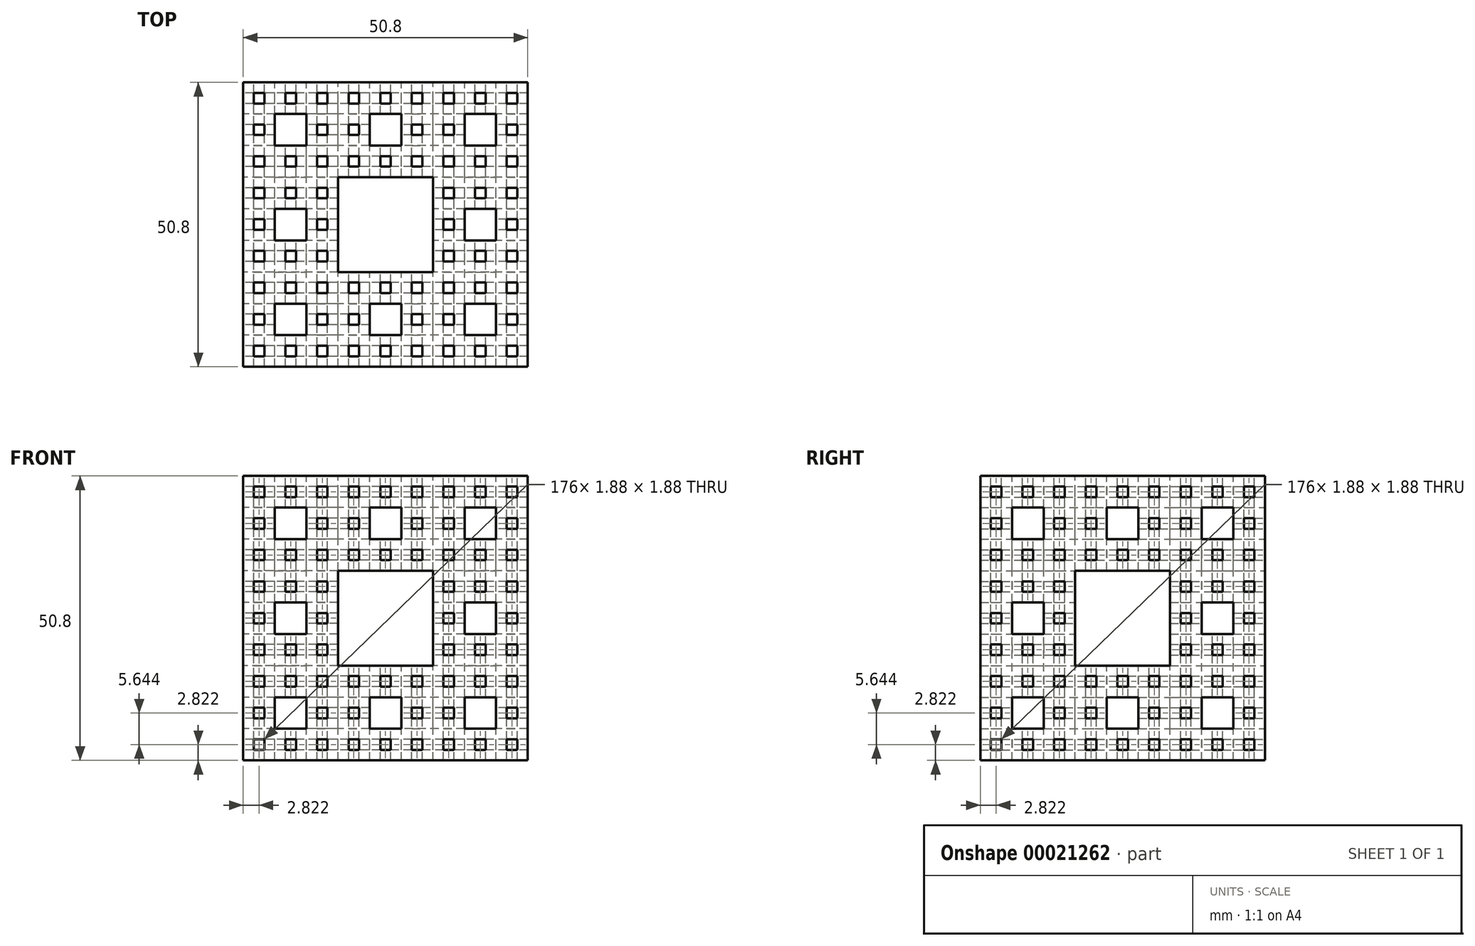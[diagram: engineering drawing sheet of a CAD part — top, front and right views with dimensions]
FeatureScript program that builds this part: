
annotation { "Feature Type Name" : "Feature", "Feature Type Description" : "" }
export const myFeature = defineFeature(function(context is Context, id is Id, definition is map)
    precondition{}
    {
        {
            var Q0;
            Q0=qCreatedBy(makeId("Front.planeOp"),FACE);
            var sketch = newSketch(context, id + "F0", { "sketchPlane" : qUnion([Q0])});
            skLineSegment(sketch, "E0.bottom", {"start": v(0, 0) * mm, "end": v(50.8, 0) * mm});
            skLineSegment(sketch, "E0.top", {"start": v(0, 50.8) * mm, "end": v(50.8, 50.8) * mm});
            skLineSegment(sketch, "E0.left", {"start": v(0, 0) * mm, "end": v(0, 50.8) * mm});
            skLineSegment(sketch, "E0.right", {"start": v(50.8, 0) * mm, "end": v(50.8, 50.8) * mm});
            skSolve(sketch);
        }
        {
            var Q0;
            Q0=makeQuery(id+"F0.imprint","IMPRINT",FACE,{"disambiguationData":[TD([[makeQuery(id+"F0.imprint","IMPRINT",EDGE,{"derivedFrom":sQuery(id+"F0.wireOp",EDGE,"E0.bottom")}),1.0]])]});
            extrude(context, id + "F1", {"entities" : qUnion([Q0]), "depth" : 50.8 * mm});
        }
        {
            var Q0;
            Q0=makeQuery(id+"F1.opExtrude","CAP_FACE",FACE,{"disambiguationData":[OSD([sQuery(id+"F0.wireOp",EDGE,"E0.bottom"),sQuery(id+"F0.wireOp",EDGE,"E0.top"),sQuery(id+"F0.wireOp",EDGE,"E0.left"),sQuery(id+"F0.wireOp",EDGE,"E0.right")])],"isStart":true});
            var sketch = newSketch(context, id + "F2", { "sketchPlane" : qUnion([Q0])});
            skLineSegment(sketch, "E1.bottom", {"start": v(-33.87, 33.87) * mm, "end": v(-16.93, 33.87) * mm});
            skLineSegment(sketch, "E1.top", {"start": v(-33.87, 16.93) * mm, "end": v(-16.93, 16.93) * mm});
            skLineSegment(sketch, "E1.left", {"start": v(-33.87, 33.87) * mm, "end": v(-33.87, 16.93) * mm});
            skLineSegment(sketch, "E1.right", {"start": v(-16.93, 33.87) * mm, "end": v(-16.93, 16.93) * mm});
            skLineSegment(sketch, "E2.bottom", {"start": v(-45.16, 11.29) * mm, "end": v(-39.51, 11.29) * mm});
            skLineSegment(sketch, "E2.top", {"start": v(-45.16, 5.64) * mm, "end": v(-39.51, 5.64) * mm});
            skLineSegment(sketch, "E2.left", {"start": v(-45.16, 11.29) * mm, "end": v(-45.16, 5.64) * mm});
            skLineSegment(sketch, "E2.right", {"start": v(-39.51, 11.29) * mm, "end": v(-39.51, 5.64) * mm});
            skLineSegment(sketch, "E3.bottom", {"start": v(-48.92, 3.76) * mm, "end": v(-47.04, 3.76) * mm});
            skLineSegment(sketch, "E3.top", {"start": v(-48.92, 1.88) * mm, "end": v(-47.04, 1.88) * mm});
            skLineSegment(sketch, "E3.left", {"start": v(-48.92, 3.76) * mm, "end": v(-48.92, 1.88) * mm});
            skLineSegment(sketch, "E3.right", {"start": v(-47.04, 3.76) * mm, "end": v(-47.04, 1.88) * mm});
            skLineSegment(sketch, "E4.0.1.0", {"start": v(-39.51, 28.22) * mm, "end": v(-39.51, 22.58) * mm});
            skLineSegment(sketch, "E4.0.1.5", {"start": v(-45.16, 28.22) * mm, "end": v(-39.51, 28.22) * mm});
            skLineSegment(sketch, "E4.0.1.6", {"start": v(-45.16, 22.58) * mm, "end": v(-39.51, 22.58) * mm});
            skLineSegment(sketch, "E4.0.1.7", {"start": v(-45.16, 28.22) * mm, "end": v(-45.16, 22.58) * mm});
            skLineSegment(sketch, "E4.0.2.0", {"start": v(-39.51, 45.16) * mm, "end": v(-39.51, 39.51) * mm});
            skLineSegment(sketch, "E4.0.2.5", {"start": v(-45.16, 45.16) * mm, "end": v(-39.51, 45.16) * mm});
            skLineSegment(sketch, "E4.0.2.6", {"start": v(-45.16, 39.51) * mm, "end": v(-39.51, 39.51) * mm});
            skLineSegment(sketch, "E4.0.2.7", {"start": v(-45.16, 45.16) * mm, "end": v(-45.16, 39.51) * mm});
            skLineSegment(sketch, "E4.1.0.0", {"start": v(-22.58, 11.29) * mm, "end": v(-22.58, 5.64) * mm});
            skLineSegment(sketch, "E4.1.0.5", {"start": v(-28.22, 11.29) * mm, "end": v(-22.58, 11.29) * mm});
            skLineSegment(sketch, "E4.1.0.6", {"start": v(-28.22, 5.64) * mm, "end": v(-22.58, 5.64) * mm});
            skLineSegment(sketch, "E4.1.0.7", {"start": v(-28.22, 11.29) * mm, "end": v(-28.22, 5.64) * mm});
            skLineSegment(sketch, "E4.1.2.0", {"start": v(-22.58, 45.16) * mm, "end": v(-22.58, 39.51) * mm});
            skLineSegment(sketch, "E4.1.2.5", {"start": v(-28.22, 45.16) * mm, "end": v(-22.58, 45.16) * mm});
            skLineSegment(sketch, "E4.1.2.6", {"start": v(-28.22, 39.51) * mm, "end": v(-22.58, 39.51) * mm});
            skLineSegment(sketch, "E4.1.2.7", {"start": v(-28.22, 45.16) * mm, "end": v(-28.22, 39.51) * mm});
            skLineSegment(sketch, "E4.2.0.0", {"start": v(-5.64, 11.29) * mm, "end": v(-5.64, 5.64) * mm});
            skLineSegment(sketch, "E4.2.0.5", {"start": v(-11.29, 11.29) * mm, "end": v(-5.64, 11.29) * mm});
            skLineSegment(sketch, "E4.2.0.6", {"start": v(-11.29, 5.64) * mm, "end": v(-5.64, 5.64) * mm});
            skLineSegment(sketch, "E4.2.0.7", {"start": v(-11.29, 11.29) * mm, "end": v(-11.29, 5.64) * mm});
            skLineSegment(sketch, "E4.2.1.0", {"start": v(-5.64, 28.22) * mm, "end": v(-5.64, 22.58) * mm});
            skLineSegment(sketch, "E4.2.1.5", {"start": v(-11.29, 28.22) * mm, "end": v(-5.64, 28.22) * mm});
            skLineSegment(sketch, "E4.2.1.6", {"start": v(-11.29, 22.58) * mm, "end": v(-5.64, 22.58) * mm});
            skLineSegment(sketch, "E4.2.1.7", {"start": v(-11.29, 28.22) * mm, "end": v(-11.29, 22.58) * mm});
            skLineSegment(sketch, "E4.2.2.0", {"start": v(-5.64, 45.16) * mm, "end": v(-5.64, 39.51) * mm});
            skLineSegment(sketch, "E4.2.2.5", {"start": v(-11.29, 45.16) * mm, "end": v(-5.64, 45.16) * mm});
            skLineSegment(sketch, "E4.2.2.6", {"start": v(-11.29, 39.51) * mm, "end": v(-5.64, 39.51) * mm});
            skLineSegment(sketch, "E4.2.2.7", {"start": v(-11.29, 45.16) * mm, "end": v(-11.29, 39.51) * mm});
            skLineSegment(sketch, "E4.direction1", {"start": v(-39.51, 5.64) * mm, "end": v(-22.58, 5.64) * mm, "construction": true});
            skLineSegment(sketch, "E4.direction2", {"start": v(-39.51, 5.64) * mm, "end": v(-39.51, 22.58) * mm, "construction": true});
            skLineSegment(sketch, "E5.0.1.2", {"start": v(-48.92, 9.4) * mm, "end": v(-47.04, 9.4) * mm});
            skLineSegment(sketch, "E5.0.1.3", {"start": v(-48.92, 7.53) * mm, "end": v(-47.04, 7.53) * mm});
            skLineSegment(sketch, "E5.0.1.4", {"start": v(-48.92, 9.4) * mm, "end": v(-48.92, 7.53) * mm});
            skLineSegment(sketch, "E5.0.1.5", {"start": v(-47.04, 9.4) * mm, "end": v(-47.04, 7.53) * mm});
            skLineSegment(sketch, "E5.0.2.2", {"start": v(-48.92, 15.05) * mm, "end": v(-47.04, 15.05) * mm});
            skLineSegment(sketch, "E5.0.2.3", {"start": v(-48.92, 13.17) * mm, "end": v(-47.04, 13.17) * mm});
            skLineSegment(sketch, "E5.0.2.4", {"start": v(-48.92, 15.05) * mm, "end": v(-48.92, 13.17) * mm});
            skLineSegment(sketch, "E5.0.2.5", {"start": v(-47.04, 15.05) * mm, "end": v(-47.04, 13.17) * mm});
            skLineSegment(sketch, "E5.0.3.2", {"start": v(-48.92, 20.7) * mm, "end": v(-47.04, 20.7) * mm});
            skLineSegment(sketch, "E5.0.3.3", {"start": v(-48.92, 18.81) * mm, "end": v(-47.04, 18.81) * mm});
            skLineSegment(sketch, "E5.0.3.4", {"start": v(-48.92, 20.7) * mm, "end": v(-48.92, 18.81) * mm});
            skLineSegment(sketch, "E5.0.3.5", {"start": v(-47.04, 20.7) * mm, "end": v(-47.04, 18.81) * mm});
            skLineSegment(sketch, "E5.0.4.2", {"start": v(-48.92, 26.34) * mm, "end": v(-47.04, 26.34) * mm});
            skLineSegment(sketch, "E5.0.4.3", {"start": v(-48.92, 24.46) * mm, "end": v(-47.04, 24.46) * mm});
            skLineSegment(sketch, "E5.0.4.4", {"start": v(-48.92, 26.34) * mm, "end": v(-48.92, 24.46) * mm});
            skLineSegment(sketch, "E5.0.4.5", {"start": v(-47.04, 26.34) * mm, "end": v(-47.04, 24.46) * mm});
            skLineSegment(sketch, "E5.0.5.2", {"start": v(-48.92, 31.99) * mm, "end": v(-47.04, 31.99) * mm});
            skLineSegment(sketch, "E5.0.5.3", {"start": v(-48.92, 30.1) * mm, "end": v(-47.04, 30.1) * mm});
            skLineSegment(sketch, "E5.0.5.4", {"start": v(-48.92, 31.99) * mm, "end": v(-48.92, 30.1) * mm});
            skLineSegment(sketch, "E5.0.5.5", {"start": v(-47.04, 31.99) * mm, "end": v(-47.04, 30.1) * mm});
            skLineSegment(sketch, "E5.0.6.2", {"start": v(-48.92, 37.63) * mm, "end": v(-47.04, 37.63) * mm});
            skLineSegment(sketch, "E5.0.6.3", {"start": v(-48.92, 35.75) * mm, "end": v(-47.04, 35.75) * mm});
            skLineSegment(sketch, "E5.0.6.4", {"start": v(-48.92, 37.63) * mm, "end": v(-48.92, 35.75) * mm});
            skLineSegment(sketch, "E5.0.6.5", {"start": v(-47.04, 37.63) * mm, "end": v(-47.04, 35.75) * mm});
            skLineSegment(sketch, "E5.0.7.2", {"start": v(-48.92, 43.27) * mm, "end": v(-47.04, 43.27) * mm});
            skLineSegment(sketch, "E5.0.7.3", {"start": v(-48.92, 41.4) * mm, "end": v(-47.04, 41.4) * mm});
            skLineSegment(sketch, "E5.0.7.4", {"start": v(-48.92, 43.27) * mm, "end": v(-48.92, 41.4) * mm});
            skLineSegment(sketch, "E5.0.7.5", {"start": v(-47.04, 43.27) * mm, "end": v(-47.04, 41.4) * mm});
            skLineSegment(sketch, "E5.0.8.2", {"start": v(-48.92, 48.92) * mm, "end": v(-47.04, 48.92) * mm});
            skLineSegment(sketch, "E5.0.8.3", {"start": v(-48.92, 47.04) * mm, "end": v(-47.04, 47.04) * mm});
            skLineSegment(sketch, "E5.0.8.4", {"start": v(-48.92, 48.92) * mm, "end": v(-48.92, 47.04) * mm});
            skLineSegment(sketch, "E5.0.8.5", {"start": v(-47.04, 48.92) * mm, "end": v(-47.04, 47.04) * mm});
            skLineSegment(sketch, "E5.1.0.2", {"start": v(-43.27, 3.76) * mm, "end": v(-41.4, 3.76) * mm});
            skLineSegment(sketch, "E5.1.0.3", {"start": v(-43.27, 1.88) * mm, "end": v(-41.4, 1.88) * mm});
            skLineSegment(sketch, "E5.1.0.4", {"start": v(-43.27, 3.76) * mm, "end": v(-43.27, 1.88) * mm});
            skLineSegment(sketch, "E5.1.0.5", {"start": v(-41.4, 3.76) * mm, "end": v(-41.4, 1.88) * mm});
            skLineSegment(sketch, "E5.1.2.2", {"start": v(-43.27, 15.05) * mm, "end": v(-41.4, 15.05) * mm});
            skLineSegment(sketch, "E5.1.2.3", {"start": v(-43.27, 13.17) * mm, "end": v(-41.4, 13.17) * mm});
            skLineSegment(sketch, "E5.1.2.4", {"start": v(-43.27, 15.05) * mm, "end": v(-43.27, 13.17) * mm});
            skLineSegment(sketch, "E5.1.2.5", {"start": v(-41.4, 15.05) * mm, "end": v(-41.4, 13.17) * mm});
            skLineSegment(sketch, "E5.1.3.2", {"start": v(-43.27, 20.7) * mm, "end": v(-41.4, 20.7) * mm});
            skLineSegment(sketch, "E5.1.3.3", {"start": v(-43.27, 18.81) * mm, "end": v(-41.4, 18.81) * mm});
            skLineSegment(sketch, "E5.1.3.4", {"start": v(-43.27, 20.7) * mm, "end": v(-43.27, 18.81) * mm});
            skLineSegment(sketch, "E5.1.3.5", {"start": v(-41.4, 20.7) * mm, "end": v(-41.4, 18.81) * mm});
            skLineSegment(sketch, "E5.1.5.2", {"start": v(-43.27, 31.99) * mm, "end": v(-41.4, 31.99) * mm});
            skLineSegment(sketch, "E5.1.5.3", {"start": v(-43.27, 30.1) * mm, "end": v(-41.4, 30.1) * mm});
            skLineSegment(sketch, "E5.1.5.4", {"start": v(-43.27, 31.99) * mm, "end": v(-43.27, 30.1) * mm});
            skLineSegment(sketch, "E5.1.5.5", {"start": v(-41.4, 31.99) * mm, "end": v(-41.4, 30.1) * mm});
            skLineSegment(sketch, "E5.1.6.2", {"start": v(-43.27, 37.63) * mm, "end": v(-41.4, 37.63) * mm});
            skLineSegment(sketch, "E5.1.6.3", {"start": v(-43.27, 35.75) * mm, "end": v(-41.4, 35.75) * mm});
            skLineSegment(sketch, "E5.1.6.4", {"start": v(-43.27, 37.63) * mm, "end": v(-43.27, 35.75) * mm});
            skLineSegment(sketch, "E5.1.6.5", {"start": v(-41.4, 37.63) * mm, "end": v(-41.4, 35.75) * mm});
            skLineSegment(sketch, "E5.1.8.2", {"start": v(-43.27, 48.92) * mm, "end": v(-41.4, 48.92) * mm});
            skLineSegment(sketch, "E5.1.8.3", {"start": v(-43.27, 47.04) * mm, "end": v(-41.4, 47.04) * mm});
            skLineSegment(sketch, "E5.1.8.4", {"start": v(-43.27, 48.92) * mm, "end": v(-43.27, 47.04) * mm});
            skLineSegment(sketch, "E5.1.8.5", {"start": v(-41.4, 48.92) * mm, "end": v(-41.4, 47.04) * mm});
            skLineSegment(sketch, "E5.2.0.2", {"start": v(-37.63, 3.76) * mm, "end": v(-35.75, 3.76) * mm});
            skLineSegment(sketch, "E5.2.0.3", {"start": v(-37.63, 1.88) * mm, "end": v(-35.75, 1.88) * mm});
            skLineSegment(sketch, "E5.2.0.4", {"start": v(-37.63, 3.76) * mm, "end": v(-37.63, 1.88) * mm});
            skLineSegment(sketch, "E5.2.0.5", {"start": v(-35.75, 3.76) * mm, "end": v(-35.75, 1.88) * mm});
            skLineSegment(sketch, "E5.2.1.2", {"start": v(-37.63, 9.4) * mm, "end": v(-35.75, 9.4) * mm});
            skLineSegment(sketch, "E5.2.1.3", {"start": v(-37.63, 7.53) * mm, "end": v(-35.75, 7.53) * mm});
            skLineSegment(sketch, "E5.2.1.4", {"start": v(-37.63, 9.4) * mm, "end": v(-37.63, 7.53) * mm});
            skLineSegment(sketch, "E5.2.1.5", {"start": v(-35.75, 9.4) * mm, "end": v(-35.75, 7.53) * mm});
            skLineSegment(sketch, "E5.2.2.2", {"start": v(-37.63, 15.05) * mm, "end": v(-35.75, 15.05) * mm});
            skLineSegment(sketch, "E5.2.2.3", {"start": v(-37.63, 13.17) * mm, "end": v(-35.75, 13.17) * mm});
            skLineSegment(sketch, "E5.2.2.4", {"start": v(-37.63, 15.05) * mm, "end": v(-37.63, 13.17) * mm});
            skLineSegment(sketch, "E5.2.2.5", {"start": v(-35.75, 15.05) * mm, "end": v(-35.75, 13.17) * mm});
            skLineSegment(sketch, "E5.2.3.2", {"start": v(-37.63, 20.7) * mm, "end": v(-35.75, 20.7) * mm});
            skLineSegment(sketch, "E5.2.3.3", {"start": v(-37.63, 18.81) * mm, "end": v(-35.75, 18.81) * mm});
            skLineSegment(sketch, "E5.2.3.4", {"start": v(-37.63, 20.7) * mm, "end": v(-37.63, 18.81) * mm});
            skLineSegment(sketch, "E5.2.3.5", {"start": v(-35.75, 20.7) * mm, "end": v(-35.75, 18.81) * mm});
            skLineSegment(sketch, "E5.2.4.2", {"start": v(-37.63, 26.34) * mm, "end": v(-35.75, 26.34) * mm});
            skLineSegment(sketch, "E5.2.4.3", {"start": v(-37.63, 24.46) * mm, "end": v(-35.75, 24.46) * mm});
            skLineSegment(sketch, "E5.2.4.4", {"start": v(-37.63, 26.34) * mm, "end": v(-37.63, 24.46) * mm});
            skLineSegment(sketch, "E5.2.4.5", {"start": v(-35.75, 26.34) * mm, "end": v(-35.75, 24.46) * mm});
            skLineSegment(sketch, "E5.2.5.2", {"start": v(-37.63, 31.99) * mm, "end": v(-35.75, 31.99) * mm});
            skLineSegment(sketch, "E5.2.5.3", {"start": v(-37.63, 30.1) * mm, "end": v(-35.75, 30.1) * mm});
            skLineSegment(sketch, "E5.2.5.4", {"start": v(-37.63, 31.99) * mm, "end": v(-37.63, 30.1) * mm});
            skLineSegment(sketch, "E5.2.5.5", {"start": v(-35.75, 31.99) * mm, "end": v(-35.75, 30.1) * mm});
            skLineSegment(sketch, "E5.2.6.2", {"start": v(-37.63, 37.63) * mm, "end": v(-35.75, 37.63) * mm});
            skLineSegment(sketch, "E5.2.6.3", {"start": v(-37.63, 35.75) * mm, "end": v(-35.75, 35.75) * mm});
            skLineSegment(sketch, "E5.2.6.4", {"start": v(-37.63, 37.63) * mm, "end": v(-37.63, 35.75) * mm});
            skLineSegment(sketch, "E5.2.6.5", {"start": v(-35.75, 37.63) * mm, "end": v(-35.75, 35.75) * mm});
            skLineSegment(sketch, "E5.2.7.2", {"start": v(-37.63, 43.27) * mm, "end": v(-35.75, 43.27) * mm});
            skLineSegment(sketch, "E5.2.7.3", {"start": v(-37.63, 41.4) * mm, "end": v(-35.75, 41.4) * mm});
            skLineSegment(sketch, "E5.2.7.4", {"start": v(-37.63, 43.27) * mm, "end": v(-37.63, 41.4) * mm});
            skLineSegment(sketch, "E5.2.7.5", {"start": v(-35.75, 43.27) * mm, "end": v(-35.75, 41.4) * mm});
            skLineSegment(sketch, "E5.2.8.2", {"start": v(-37.63, 48.92) * mm, "end": v(-35.75, 48.92) * mm});
            skLineSegment(sketch, "E5.2.8.3", {"start": v(-37.63, 47.04) * mm, "end": v(-35.75, 47.04) * mm});
            skLineSegment(sketch, "E5.2.8.4", {"start": v(-37.63, 48.92) * mm, "end": v(-37.63, 47.04) * mm});
            skLineSegment(sketch, "E5.2.8.5", {"start": v(-35.75, 48.92) * mm, "end": v(-35.75, 47.04) * mm});
            skLineSegment(sketch, "E5.3.0.2", {"start": v(-31.99, 3.76) * mm, "end": v(-30.1, 3.76) * mm});
            skLineSegment(sketch, "E5.3.0.3", {"start": v(-31.99, 1.88) * mm, "end": v(-30.1, 1.88) * mm});
            skLineSegment(sketch, "E5.3.0.4", {"start": v(-31.99, 3.76) * mm, "end": v(-31.99, 1.88) * mm});
            skLineSegment(sketch, "E5.3.0.5", {"start": v(-30.1, 3.76) * mm, "end": v(-30.1, 1.88) * mm});
            skLineSegment(sketch, "E5.3.1.2", {"start": v(-31.99, 9.4) * mm, "end": v(-30.1, 9.4) * mm});
            skLineSegment(sketch, "E5.3.1.3", {"start": v(-31.99, 7.53) * mm, "end": v(-30.1, 7.53) * mm});
            skLineSegment(sketch, "E5.3.1.4", {"start": v(-31.99, 9.4) * mm, "end": v(-31.99, 7.53) * mm});
            skLineSegment(sketch, "E5.3.1.5", {"start": v(-30.1, 9.4) * mm, "end": v(-30.1, 7.53) * mm});
            skLineSegment(sketch, "E5.3.2.2", {"start": v(-31.99, 15.05) * mm, "end": v(-30.1, 15.05) * mm});
            skLineSegment(sketch, "E5.3.2.3", {"start": v(-31.99, 13.17) * mm, "end": v(-30.1, 13.17) * mm});
            skLineSegment(sketch, "E5.3.2.4", {"start": v(-31.99, 15.05) * mm, "end": v(-31.99, 13.17) * mm});
            skLineSegment(sketch, "E5.3.2.5", {"start": v(-30.1, 15.05) * mm, "end": v(-30.1, 13.17) * mm});
            skLineSegment(sketch, "E5.3.6.2", {"start": v(-31.99, 37.63) * mm, "end": v(-30.1, 37.63) * mm});
            skLineSegment(sketch, "E5.3.6.3", {"start": v(-31.99, 35.75) * mm, "end": v(-30.1, 35.75) * mm});
            skLineSegment(sketch, "E5.3.6.4", {"start": v(-31.99, 37.63) * mm, "end": v(-31.99, 35.75) * mm});
            skLineSegment(sketch, "E5.3.6.5", {"start": v(-30.1, 37.63) * mm, "end": v(-30.1, 35.75) * mm});
            skLineSegment(sketch, "E5.3.7.2", {"start": v(-31.99, 43.27) * mm, "end": v(-30.1, 43.27) * mm});
            skLineSegment(sketch, "E5.3.7.3", {"start": v(-31.99, 41.4) * mm, "end": v(-30.1, 41.4) * mm});
            skLineSegment(sketch, "E5.3.7.4", {"start": v(-31.99, 43.27) * mm, "end": v(-31.99, 41.4) * mm});
            skLineSegment(sketch, "E5.3.7.5", {"start": v(-30.1, 43.27) * mm, "end": v(-30.1, 41.4) * mm});
            skLineSegment(sketch, "E5.3.8.2", {"start": v(-31.99, 48.92) * mm, "end": v(-30.1, 48.92) * mm});
            skLineSegment(sketch, "E5.3.8.3", {"start": v(-31.99, 47.04) * mm, "end": v(-30.1, 47.04) * mm});
            skLineSegment(sketch, "E5.3.8.4", {"start": v(-31.99, 48.92) * mm, "end": v(-31.99, 47.04) * mm});
            skLineSegment(sketch, "E5.3.8.5", {"start": v(-30.1, 48.92) * mm, "end": v(-30.1, 47.04) * mm});
            skLineSegment(sketch, "E5.4.0.2", {"start": v(-26.34, 3.76) * mm, "end": v(-24.46, 3.76) * mm});
            skLineSegment(sketch, "E5.4.0.3", {"start": v(-26.34, 1.88) * mm, "end": v(-24.46, 1.88) * mm});
            skLineSegment(sketch, "E5.4.0.4", {"start": v(-26.34, 3.76) * mm, "end": v(-26.34, 1.88) * mm});
            skLineSegment(sketch, "E5.4.0.5", {"start": v(-24.46, 3.76) * mm, "end": v(-24.46, 1.88) * mm});
            skLineSegment(sketch, "E5.4.2.2", {"start": v(-26.34, 15.05) * mm, "end": v(-24.46, 15.05) * mm});
            skLineSegment(sketch, "E5.4.2.3", {"start": v(-26.34, 13.17) * mm, "end": v(-24.46, 13.17) * mm});
            skLineSegment(sketch, "E5.4.2.4", {"start": v(-26.34, 15.05) * mm, "end": v(-26.34, 13.17) * mm});
            skLineSegment(sketch, "E5.4.2.5", {"start": v(-24.46, 15.05) * mm, "end": v(-24.46, 13.17) * mm});
            skLineSegment(sketch, "E5.4.6.2", {"start": v(-26.34, 37.63) * mm, "end": v(-24.46, 37.63) * mm});
            skLineSegment(sketch, "E5.4.6.3", {"start": v(-26.34, 35.75) * mm, "end": v(-24.46, 35.75) * mm});
            skLineSegment(sketch, "E5.4.6.4", {"start": v(-26.34, 37.63) * mm, "end": v(-26.34, 35.75) * mm});
            skLineSegment(sketch, "E5.4.6.5", {"start": v(-24.46, 37.63) * mm, "end": v(-24.46, 35.75) * mm});
            skLineSegment(sketch, "E5.4.8.2", {"start": v(-26.34, 48.92) * mm, "end": v(-24.46, 48.92) * mm});
            skLineSegment(sketch, "E5.4.8.3", {"start": v(-26.34, 47.04) * mm, "end": v(-24.46, 47.04) * mm});
            skLineSegment(sketch, "E5.4.8.4", {"start": v(-26.34, 48.92) * mm, "end": v(-26.34, 47.04) * mm});
            skLineSegment(sketch, "E5.4.8.5", {"start": v(-24.46, 48.92) * mm, "end": v(-24.46, 47.04) * mm});
            skLineSegment(sketch, "E5.5.0.2", {"start": v(-20.7, 3.76) * mm, "end": v(-18.81, 3.76) * mm});
            skLineSegment(sketch, "E5.5.0.3", {"start": v(-20.7, 1.88) * mm, "end": v(-18.81, 1.88) * mm});
            skLineSegment(sketch, "E5.5.0.4", {"start": v(-20.7, 3.76) * mm, "end": v(-20.7, 1.88) * mm});
            skLineSegment(sketch, "E5.5.0.5", {"start": v(-18.81, 3.76) * mm, "end": v(-18.81, 1.88) * mm});
            skLineSegment(sketch, "E5.5.1.2", {"start": v(-20.7, 9.4) * mm, "end": v(-18.81, 9.4) * mm});
            skLineSegment(sketch, "E5.5.1.3", {"start": v(-20.7, 7.53) * mm, "end": v(-18.81, 7.53) * mm});
            skLineSegment(sketch, "E5.5.1.4", {"start": v(-20.7, 9.4) * mm, "end": v(-20.7, 7.53) * mm});
            skLineSegment(sketch, "E5.5.1.5", {"start": v(-18.81, 9.4) * mm, "end": v(-18.81, 7.53) * mm});
            skLineSegment(sketch, "E5.5.2.2", {"start": v(-20.7, 15.05) * mm, "end": v(-18.81, 15.05) * mm});
            skLineSegment(sketch, "E5.5.2.3", {"start": v(-20.7, 13.17) * mm, "end": v(-18.81, 13.17) * mm});
            skLineSegment(sketch, "E5.5.2.4", {"start": v(-20.7, 15.05) * mm, "end": v(-20.7, 13.17) * mm});
            skLineSegment(sketch, "E5.5.2.5", {"start": v(-18.81, 15.05) * mm, "end": v(-18.81, 13.17) * mm});
            skLineSegment(sketch, "E5.5.6.2", {"start": v(-20.7, 37.63) * mm, "end": v(-18.81, 37.63) * mm});
            skLineSegment(sketch, "E5.5.6.3", {"start": v(-20.7, 35.75) * mm, "end": v(-18.81, 35.75) * mm});
            skLineSegment(sketch, "E5.5.6.4", {"start": v(-20.7, 37.63) * mm, "end": v(-20.7, 35.75) * mm});
            skLineSegment(sketch, "E5.5.6.5", {"start": v(-18.81, 37.63) * mm, "end": v(-18.81, 35.75) * mm});
            skLineSegment(sketch, "E5.5.7.2", {"start": v(-20.7, 43.27) * mm, "end": v(-18.81, 43.27) * mm});
            skLineSegment(sketch, "E5.5.7.3", {"start": v(-20.7, 41.4) * mm, "end": v(-18.81, 41.4) * mm});
            skLineSegment(sketch, "E5.5.7.4", {"start": v(-20.7, 43.27) * mm, "end": v(-20.7, 41.4) * mm});
            skLineSegment(sketch, "E5.5.7.5", {"start": v(-18.81, 43.27) * mm, "end": v(-18.81, 41.4) * mm});
            skLineSegment(sketch, "E5.5.8.2", {"start": v(-20.7, 48.92) * mm, "end": v(-18.81, 48.92) * mm});
            skLineSegment(sketch, "E5.5.8.3", {"start": v(-20.7, 47.04) * mm, "end": v(-18.81, 47.04) * mm});
            skLineSegment(sketch, "E5.5.8.4", {"start": v(-20.7, 48.92) * mm, "end": v(-20.7, 47.04) * mm});
            skLineSegment(sketch, "E5.5.8.5", {"start": v(-18.81, 48.92) * mm, "end": v(-18.81, 47.04) * mm});
            skLineSegment(sketch, "E5.6.0.2", {"start": v(-15.05, 3.76) * mm, "end": v(-13.17, 3.76) * mm});
            skLineSegment(sketch, "E5.6.0.3", {"start": v(-15.05, 1.88) * mm, "end": v(-13.17, 1.88) * mm});
            skLineSegment(sketch, "E5.6.0.4", {"start": v(-15.05, 3.76) * mm, "end": v(-15.05, 1.88) * mm});
            skLineSegment(sketch, "E5.6.0.5", {"start": v(-13.17, 3.76) * mm, "end": v(-13.17, 1.88) * mm});
            skLineSegment(sketch, "E5.6.1.2", {"start": v(-15.05, 9.4) * mm, "end": v(-13.17, 9.4) * mm});
            skLineSegment(sketch, "E5.6.1.3", {"start": v(-15.05, 7.53) * mm, "end": v(-13.17, 7.53) * mm});
            skLineSegment(sketch, "E5.6.1.4", {"start": v(-15.05, 9.4) * mm, "end": v(-15.05, 7.53) * mm});
            skLineSegment(sketch, "E5.6.1.5", {"start": v(-13.17, 9.4) * mm, "end": v(-13.17, 7.53) * mm});
            skLineSegment(sketch, "E5.6.2.2", {"start": v(-15.05, 15.05) * mm, "end": v(-13.17, 15.05) * mm});
            skLineSegment(sketch, "E5.6.2.3", {"start": v(-15.05, 13.17) * mm, "end": v(-13.17, 13.17) * mm});
            skLineSegment(sketch, "E5.6.2.4", {"start": v(-15.05, 15.05) * mm, "end": v(-15.05, 13.17) * mm});
            skLineSegment(sketch, "E5.6.2.5", {"start": v(-13.17, 15.05) * mm, "end": v(-13.17, 13.17) * mm});
            skLineSegment(sketch, "E5.6.3.2", {"start": v(-15.05, 20.7) * mm, "end": v(-13.17, 20.7) * mm});
            skLineSegment(sketch, "E5.6.3.3", {"start": v(-15.05, 18.81) * mm, "end": v(-13.17, 18.81) * mm});
            skLineSegment(sketch, "E5.6.3.4", {"start": v(-15.05, 20.7) * mm, "end": v(-15.05, 18.81) * mm});
            skLineSegment(sketch, "E5.6.3.5", {"start": v(-13.17, 20.7) * mm, "end": v(-13.17, 18.81) * mm});
            skLineSegment(sketch, "E5.6.4.2", {"start": v(-15.05, 26.34) * mm, "end": v(-13.17, 26.34) * mm});
            skLineSegment(sketch, "E5.6.4.3", {"start": v(-15.05, 24.46) * mm, "end": v(-13.17, 24.46) * mm});
            skLineSegment(sketch, "E5.6.4.4", {"start": v(-15.05, 26.34) * mm, "end": v(-15.05, 24.46) * mm});
            skLineSegment(sketch, "E5.6.4.5", {"start": v(-13.17, 26.34) * mm, "end": v(-13.17, 24.46) * mm});
            skLineSegment(sketch, "E5.6.5.2", {"start": v(-15.05, 31.99) * mm, "end": v(-13.17, 31.99) * mm});
            skLineSegment(sketch, "E5.6.5.3", {"start": v(-15.05, 30.1) * mm, "end": v(-13.17, 30.1) * mm});
            skLineSegment(sketch, "E5.6.5.4", {"start": v(-15.05, 31.99) * mm, "end": v(-15.05, 30.1) * mm});
            skLineSegment(sketch, "E5.6.5.5", {"start": v(-13.17, 31.99) * mm, "end": v(-13.17, 30.1) * mm});
            skLineSegment(sketch, "E5.6.6.2", {"start": v(-15.05, 37.63) * mm, "end": v(-13.17, 37.63) * mm});
            skLineSegment(sketch, "E5.6.6.3", {"start": v(-15.05, 35.75) * mm, "end": v(-13.17, 35.75) * mm});
            skLineSegment(sketch, "E5.6.6.4", {"start": v(-15.05, 37.63) * mm, "end": v(-15.05, 35.75) * mm});
            skLineSegment(sketch, "E5.6.6.5", {"start": v(-13.17, 37.63) * mm, "end": v(-13.17, 35.75) * mm});
            skLineSegment(sketch, "E5.6.7.2", {"start": v(-15.05, 43.27) * mm, "end": v(-13.17, 43.27) * mm});
            skLineSegment(sketch, "E5.6.7.3", {"start": v(-15.05, 41.4) * mm, "end": v(-13.17, 41.4) * mm});
            skLineSegment(sketch, "E5.6.7.4", {"start": v(-15.05, 43.27) * mm, "end": v(-15.05, 41.4) * mm});
            skLineSegment(sketch, "E5.6.7.5", {"start": v(-13.17, 43.27) * mm, "end": v(-13.17, 41.4) * mm});
            skLineSegment(sketch, "E5.6.8.2", {"start": v(-15.05, 48.92) * mm, "end": v(-13.17, 48.92) * mm});
            skLineSegment(sketch, "E5.6.8.3", {"start": v(-15.05, 47.04) * mm, "end": v(-13.17, 47.04) * mm});
            skLineSegment(sketch, "E5.6.8.4", {"start": v(-15.05, 48.92) * mm, "end": v(-15.05, 47.04) * mm});
            skLineSegment(sketch, "E5.6.8.5", {"start": v(-13.17, 48.92) * mm, "end": v(-13.17, 47.04) * mm});
            skLineSegment(sketch, "E5.7.0.2", {"start": v(-9.4, 3.76) * mm, "end": v(-7.53, 3.76) * mm});
            skLineSegment(sketch, "E5.7.0.3", {"start": v(-9.4, 1.88) * mm, "end": v(-7.53, 1.88) * mm});
            skLineSegment(sketch, "E5.7.0.4", {"start": v(-9.4, 3.76) * mm, "end": v(-9.4, 1.88) * mm});
            skLineSegment(sketch, "E5.7.0.5", {"start": v(-7.53, 3.76) * mm, "end": v(-7.53, 1.88) * mm});
            skLineSegment(sketch, "E5.7.2.2", {"start": v(-9.4, 15.05) * mm, "end": v(-7.53, 15.05) * mm});
            skLineSegment(sketch, "E5.7.2.3", {"start": v(-9.4, 13.17) * mm, "end": v(-7.53, 13.17) * mm});
            skLineSegment(sketch, "E5.7.2.4", {"start": v(-9.4, 15.05) * mm, "end": v(-9.4, 13.17) * mm});
            skLineSegment(sketch, "E5.7.2.5", {"start": v(-7.53, 15.05) * mm, "end": v(-7.53, 13.17) * mm});
            skLineSegment(sketch, "E5.7.3.2", {"start": v(-9.4, 20.7) * mm, "end": v(-7.53, 20.7) * mm});
            skLineSegment(sketch, "E5.7.3.3", {"start": v(-9.4, 18.81) * mm, "end": v(-7.53, 18.81) * mm});
            skLineSegment(sketch, "E5.7.3.4", {"start": v(-9.4, 20.7) * mm, "end": v(-9.4, 18.81) * mm});
            skLineSegment(sketch, "E5.7.3.5", {"start": v(-7.53, 20.7) * mm, "end": v(-7.53, 18.81) * mm});
            skLineSegment(sketch, "E5.7.5.2", {"start": v(-9.4, 31.99) * mm, "end": v(-7.53, 31.99) * mm});
            skLineSegment(sketch, "E5.7.5.3", {"start": v(-9.4, 30.1) * mm, "end": v(-7.53, 30.1) * mm});
            skLineSegment(sketch, "E5.7.5.4", {"start": v(-9.4, 31.99) * mm, "end": v(-9.4, 30.1) * mm});
            skLineSegment(sketch, "E5.7.5.5", {"start": v(-7.53, 31.99) * mm, "end": v(-7.53, 30.1) * mm});
            skLineSegment(sketch, "E5.7.6.2", {"start": v(-9.4, 37.63) * mm, "end": v(-7.53, 37.63) * mm});
            skLineSegment(sketch, "E5.7.6.3", {"start": v(-9.4, 35.75) * mm, "end": v(-7.53, 35.75) * mm});
            skLineSegment(sketch, "E5.7.6.4", {"start": v(-9.4, 37.63) * mm, "end": v(-9.4, 35.75) * mm});
            skLineSegment(sketch, "E5.7.6.5", {"start": v(-7.53, 37.63) * mm, "end": v(-7.53, 35.75) * mm});
            skLineSegment(sketch, "E5.7.8.2", {"start": v(-9.4, 48.92) * mm, "end": v(-7.53, 48.92) * mm});
            skLineSegment(sketch, "E5.7.8.3", {"start": v(-9.4, 47.04) * mm, "end": v(-7.53, 47.04) * mm});
            skLineSegment(sketch, "E5.7.8.4", {"start": v(-9.4, 48.92) * mm, "end": v(-9.4, 47.04) * mm});
            skLineSegment(sketch, "E5.7.8.5", {"start": v(-7.53, 48.92) * mm, "end": v(-7.53, 47.04) * mm});
            skLineSegment(sketch, "E5.8.0.2", {"start": v(-3.76, 3.76) * mm, "end": v(-1.88, 3.76) * mm});
            skLineSegment(sketch, "E5.8.0.3", {"start": v(-3.76, 1.88) * mm, "end": v(-1.88, 1.88) * mm});
            skLineSegment(sketch, "E5.8.0.4", {"start": v(-3.76, 3.76) * mm, "end": v(-3.76, 1.88) * mm});
            skLineSegment(sketch, "E5.8.0.5", {"start": v(-1.88, 3.76) * mm, "end": v(-1.88, 1.88) * mm});
            skLineSegment(sketch, "E5.8.1.2", {"start": v(-3.76, 9.4) * mm, "end": v(-1.88, 9.4) * mm});
            skLineSegment(sketch, "E5.8.1.3", {"start": v(-3.76, 7.53) * mm, "end": v(-1.88, 7.53) * mm});
            skLineSegment(sketch, "E5.8.1.4", {"start": v(-3.76, 9.4) * mm, "end": v(-3.76, 7.53) * mm});
            skLineSegment(sketch, "E5.8.1.5", {"start": v(-1.88, 9.4) * mm, "end": v(-1.88, 7.53) * mm});
            skLineSegment(sketch, "E5.8.2.2", {"start": v(-3.76, 15.05) * mm, "end": v(-1.88, 15.05) * mm});
            skLineSegment(sketch, "E5.8.2.3", {"start": v(-3.76, 13.17) * mm, "end": v(-1.88, 13.17) * mm});
            skLineSegment(sketch, "E5.8.2.4", {"start": v(-3.76, 15.05) * mm, "end": v(-3.76, 13.17) * mm});
            skLineSegment(sketch, "E5.8.2.5", {"start": v(-1.88, 15.05) * mm, "end": v(-1.88, 13.17) * mm});
            skLineSegment(sketch, "E5.8.3.2", {"start": v(-3.76, 20.7) * mm, "end": v(-1.88, 20.7) * mm});
            skLineSegment(sketch, "E5.8.3.3", {"start": v(-3.76, 18.81) * mm, "end": v(-1.88, 18.81) * mm});
            skLineSegment(sketch, "E5.8.3.4", {"start": v(-3.76, 20.7) * mm, "end": v(-3.76, 18.81) * mm});
            skLineSegment(sketch, "E5.8.3.5", {"start": v(-1.88, 20.7) * mm, "end": v(-1.88, 18.81) * mm});
            skLineSegment(sketch, "E5.8.4.2", {"start": v(-3.76, 26.34) * mm, "end": v(-1.88, 26.34) * mm});
            skLineSegment(sketch, "E5.8.4.3", {"start": v(-3.76, 24.46) * mm, "end": v(-1.88, 24.46) * mm});
            skLineSegment(sketch, "E5.8.4.4", {"start": v(-3.76, 26.34) * mm, "end": v(-3.76, 24.46) * mm});
            skLineSegment(sketch, "E5.8.4.5", {"start": v(-1.88, 26.34) * mm, "end": v(-1.88, 24.46) * mm});
            skLineSegment(sketch, "E5.8.5.2", {"start": v(-3.76, 31.99) * mm, "end": v(-1.88, 31.99) * mm});
            skLineSegment(sketch, "E5.8.5.3", {"start": v(-3.76, 30.1) * mm, "end": v(-1.88, 30.1) * mm});
            skLineSegment(sketch, "E5.8.5.4", {"start": v(-3.76, 31.99) * mm, "end": v(-3.76, 30.1) * mm});
            skLineSegment(sketch, "E5.8.5.5", {"start": v(-1.88, 31.99) * mm, "end": v(-1.88, 30.1) * mm});
            skLineSegment(sketch, "E5.8.6.2", {"start": v(-3.76, 37.63) * mm, "end": v(-1.88, 37.63) * mm});
            skLineSegment(sketch, "E5.8.6.3", {"start": v(-3.76, 35.75) * mm, "end": v(-1.88, 35.75) * mm});
            skLineSegment(sketch, "E5.8.6.4", {"start": v(-3.76, 37.63) * mm, "end": v(-3.76, 35.75) * mm});
            skLineSegment(sketch, "E5.8.6.5", {"start": v(-1.88, 37.63) * mm, "end": v(-1.88, 35.75) * mm});
            skLineSegment(sketch, "E5.8.7.2", {"start": v(-3.76, 43.27) * mm, "end": v(-1.88, 43.27) * mm});
            skLineSegment(sketch, "E5.8.7.3", {"start": v(-3.76, 41.4) * mm, "end": v(-1.88, 41.4) * mm});
            skLineSegment(sketch, "E5.8.7.4", {"start": v(-3.76, 43.27) * mm, "end": v(-3.76, 41.4) * mm});
            skLineSegment(sketch, "E5.8.7.5", {"start": v(-1.88, 43.27) * mm, "end": v(-1.88, 41.4) * mm});
            skLineSegment(sketch, "E5.8.8.2", {"start": v(-3.76, 48.92) * mm, "end": v(-1.88, 48.92) * mm});
            skLineSegment(sketch, "E5.8.8.3", {"start": v(-3.76, 47.04) * mm, "end": v(-1.88, 47.04) * mm});
            skLineSegment(sketch, "E5.8.8.4", {"start": v(-3.76, 48.92) * mm, "end": v(-3.76, 47.04) * mm});
            skLineSegment(sketch, "E5.8.8.5", {"start": v(-1.88, 48.92) * mm, "end": v(-1.88, 47.04) * mm});
            skLineSegment(sketch, "E5.direction1", {"start": v(-47.04, 3.76) * mm, "end": v(-41.4, 3.76) * mm, "construction": true});
            skLineSegment(sketch, "E5.direction2", {"start": v(-47.04, 3.76) * mm, "end": v(-47.04, 9.4) * mm, "construction": true});
            skSolve(sketch);
        }
        {
            var Q0;
            Q0 = qSketchRegion(id + "F2", true);
            extrude(context, id + "F3", {"entities" : qUnion([Q0]), "operationType" : NewBodyOperationType.REMOVE, "endBound" : BoundingType.THROUGH_ALL, "oppositeDirection" : true, "depth" : 25.4 * mm});
        }
        {
            var Q0;
            Q0=makeQuery(id+"F1.opExtrude","SWEPT_FACE",FACE,{"disambiguationData":[OSD([sQuery(id+"F0.wireOp",EDGE,"E0.top")])]});
            var sketch = newSketch(context, id + "F4", { "sketchPlane" : qUnion([Q0])});
            skLineSegment(sketch, "E6.bottom", {"start": v(33.87, -16.93) * mm, "end": v(16.93, -16.93) * mm});
            skLineSegment(sketch, "E6.top", {"start": v(33.87, -33.87) * mm, "end": v(16.93, -33.87) * mm});
            skLineSegment(sketch, "E6.left", {"start": v(33.87, -16.93) * mm, "end": v(33.87, -33.87) * mm});
            skLineSegment(sketch, "E6.right", {"start": v(16.93, -16.93) * mm, "end": v(16.93, -33.87) * mm});
            skLineSegment(sketch, "E7.bottom", {"start": v(5.64, -39.51) * mm, "end": v(11.29, -39.51) * mm});
            skLineSegment(sketch, "E7.top", {"start": v(5.64, -45.16) * mm, "end": v(11.29, -45.16) * mm});
            skLineSegment(sketch, "E7.left", {"start": v(5.64, -39.51) * mm, "end": v(5.64, -45.16) * mm});
            skLineSegment(sketch, "E7.right", {"start": v(11.29, -39.51) * mm, "end": v(11.29, -45.16) * mm});
            skLineSegment(sketch, "E8.0.1.1", {"start": v(11.29, -22.58) * mm, "end": v(11.29, -28.22) * mm});
            skLineSegment(sketch, "E8.0.1.5", {"start": v(5.64, -28.22) * mm, "end": v(11.29, -28.22) * mm});
            skLineSegment(sketch, "E8.0.1.6", {"start": v(5.64, -22.58) * mm, "end": v(5.64, -28.22) * mm});
            skLineSegment(sketch, "E8.0.1.7", {"start": v(5.64, -22.58) * mm, "end": v(11.29, -22.58) * mm});
            skLineSegment(sketch, "E8.0.2.1", {"start": v(11.29, -5.64) * mm, "end": v(11.29, -11.29) * mm});
            skLineSegment(sketch, "E8.0.2.5", {"start": v(5.64, -11.29) * mm, "end": v(11.29, -11.29) * mm});
            skLineSegment(sketch, "E8.0.2.6", {"start": v(5.64, -5.64) * mm, "end": v(5.64, -11.29) * mm});
            skLineSegment(sketch, "E8.0.2.7", {"start": v(5.64, -5.64) * mm, "end": v(11.29, -5.64) * mm});
            skLineSegment(sketch, "E8.1.0.1", {"start": v(28.22, -39.51) * mm, "end": v(28.22, -45.16) * mm});
            skLineSegment(sketch, "E8.1.0.5", {"start": v(22.58, -45.16) * mm, "end": v(28.22, -45.16) * mm});
            skLineSegment(sketch, "E8.1.0.6", {"start": v(22.58, -39.51) * mm, "end": v(22.58, -45.16) * mm});
            skLineSegment(sketch, "E8.1.0.7", {"start": v(22.58, -39.51) * mm, "end": v(28.22, -39.51) * mm});
            skLineSegment(sketch, "E8.1.2.1", {"start": v(28.22, -5.64) * mm, "end": v(28.22, -11.29) * mm});
            skLineSegment(sketch, "E8.1.2.5", {"start": v(22.58, -11.29) * mm, "end": v(28.22, -11.29) * mm});
            skLineSegment(sketch, "E8.1.2.6", {"start": v(22.58, -5.64) * mm, "end": v(22.58, -11.29) * mm});
            skLineSegment(sketch, "E8.1.2.7", {"start": v(22.58, -5.64) * mm, "end": v(28.22, -5.64) * mm});
            skLineSegment(sketch, "E8.2.0.1", {"start": v(45.16, -39.51) * mm, "end": v(45.16, -45.16) * mm});
            skLineSegment(sketch, "E8.2.0.5", {"start": v(39.51, -45.16) * mm, "end": v(45.16, -45.16) * mm});
            skLineSegment(sketch, "E8.2.0.6", {"start": v(39.51, -39.51) * mm, "end": v(39.51, -45.16) * mm});
            skLineSegment(sketch, "E8.2.0.7", {"start": v(39.51, -39.51) * mm, "end": v(45.16, -39.51) * mm});
            skLineSegment(sketch, "E8.2.1.1", {"start": v(45.16, -22.58) * mm, "end": v(45.16, -28.22) * mm});
            skLineSegment(sketch, "E8.2.1.5", {"start": v(39.51, -28.22) * mm, "end": v(45.16, -28.22) * mm});
            skLineSegment(sketch, "E8.2.1.6", {"start": v(39.51, -22.58) * mm, "end": v(39.51, -28.22) * mm});
            skLineSegment(sketch, "E8.2.1.7", {"start": v(39.51, -22.58) * mm, "end": v(45.16, -22.58) * mm});
            skLineSegment(sketch, "E8.2.2.1", {"start": v(45.16, -5.64) * mm, "end": v(45.16, -11.29) * mm});
            skLineSegment(sketch, "E8.2.2.5", {"start": v(39.51, -11.29) * mm, "end": v(45.16, -11.29) * mm});
            skLineSegment(sketch, "E8.2.2.6", {"start": v(39.51, -5.64) * mm, "end": v(39.51, -11.29) * mm});
            skLineSegment(sketch, "E8.2.2.7", {"start": v(39.51, -5.64) * mm, "end": v(45.16, -5.64) * mm});
            skLineSegment(sketch, "E8.direction1", {"start": v(11.29, -45.16) * mm, "end": v(28.22, -45.16) * mm, "construction": true});
            skLineSegment(sketch, "E8.direction2", {"start": v(11.29, -45.16) * mm, "end": v(11.29, -28.22) * mm, "construction": true});
            skLineSegment(sketch, "E9.bottom", {"start": v(1.88, -47.04) * mm, "end": v(3.76, -47.04) * mm});
            skLineSegment(sketch, "E9.top", {"start": v(1.88, -48.92) * mm, "end": v(3.76, -48.92) * mm});
            skLineSegment(sketch, "E9.left", {"start": v(1.88, -47.04) * mm, "end": v(1.88, -48.92) * mm});
            skLineSegment(sketch, "E9.right", {"start": v(3.76, -47.04) * mm, "end": v(3.76, -48.92) * mm});
            skLineSegment(sketch, "E10.0.1.0", {"start": v(1.88, -41.4) * mm, "end": v(1.88, -43.27) * mm});
            skLineSegment(sketch, "E10.0.1.4", {"start": v(3.76, -41.4) * mm, "end": v(3.76, -43.27) * mm});
            skLineSegment(sketch, "E10.0.1.5", {"start": v(1.88, -43.27) * mm, "end": v(3.76, -43.27) * mm});
            skLineSegment(sketch, "E10.0.1.6", {"start": v(1.88, -41.4) * mm, "end": v(3.76, -41.4) * mm});
            skLineSegment(sketch, "E10.0.2.0", {"start": v(1.88, -35.75) * mm, "end": v(1.88, -37.63) * mm});
            skLineSegment(sketch, "E10.0.2.4", {"start": v(3.76, -35.75) * mm, "end": v(3.76, -37.63) * mm});
            skLineSegment(sketch, "E10.0.2.5", {"start": v(1.88, -37.63) * mm, "end": v(3.76, -37.63) * mm});
            skLineSegment(sketch, "E10.0.2.6", {"start": v(1.88, -35.75) * mm, "end": v(3.76, -35.75) * mm});
            skLineSegment(sketch, "E10.0.3.0", {"start": v(1.88, -30.1) * mm, "end": v(1.88, -31.99) * mm});
            skLineSegment(sketch, "E10.0.3.4", {"start": v(3.76, -30.1) * mm, "end": v(3.76, -31.99) * mm});
            skLineSegment(sketch, "E10.0.3.5", {"start": v(1.88, -31.99) * mm, "end": v(3.76, -31.99) * mm});
            skLineSegment(sketch, "E10.0.3.6", {"start": v(1.88, -30.1) * mm, "end": v(3.76, -30.1) * mm});
            skLineSegment(sketch, "E10.0.4.0", {"start": v(1.88, -24.46) * mm, "end": v(1.88, -26.34) * mm});
            skLineSegment(sketch, "E10.0.4.4", {"start": v(3.76, -24.46) * mm, "end": v(3.76, -26.34) * mm});
            skLineSegment(sketch, "E10.0.4.5", {"start": v(1.88, -26.34) * mm, "end": v(3.76, -26.34) * mm});
            skLineSegment(sketch, "E10.0.4.6", {"start": v(1.88, -24.46) * mm, "end": v(3.76, -24.46) * mm});
            skLineSegment(sketch, "E10.0.5.0", {"start": v(1.88, -18.81) * mm, "end": v(1.88, -20.7) * mm});
            skLineSegment(sketch, "E10.0.5.4", {"start": v(3.76, -18.81) * mm, "end": v(3.76, -20.7) * mm});
            skLineSegment(sketch, "E10.0.5.5", {"start": v(1.88, -20.7) * mm, "end": v(3.76, -20.7) * mm});
            skLineSegment(sketch, "E10.0.5.6", {"start": v(1.88, -18.81) * mm, "end": v(3.76, -18.81) * mm});
            skLineSegment(sketch, "E10.0.6.0", {"start": v(1.88, -13.17) * mm, "end": v(1.88, -15.05) * mm});
            skLineSegment(sketch, "E10.0.6.4", {"start": v(3.76, -13.17) * mm, "end": v(3.76, -15.05) * mm});
            skLineSegment(sketch, "E10.0.6.5", {"start": v(1.88, -15.05) * mm, "end": v(3.76, -15.05) * mm});
            skLineSegment(sketch, "E10.0.6.6", {"start": v(1.88, -13.17) * mm, "end": v(3.76, -13.17) * mm});
            skLineSegment(sketch, "E10.0.7.0", {"start": v(1.88, -7.53) * mm, "end": v(1.88, -9.4) * mm});
            skLineSegment(sketch, "E10.0.7.4", {"start": v(3.76, -7.53) * mm, "end": v(3.76, -9.4) * mm});
            skLineSegment(sketch, "E10.0.7.5", {"start": v(1.88, -9.4) * mm, "end": v(3.76, -9.4) * mm});
            skLineSegment(sketch, "E10.0.7.6", {"start": v(1.88, -7.53) * mm, "end": v(3.76, -7.53) * mm});
            skLineSegment(sketch, "E10.0.8.0", {"start": v(1.88, -1.88) * mm, "end": v(1.88, -3.76) * mm});
            skLineSegment(sketch, "E10.0.8.4", {"start": v(3.76, -1.88) * mm, "end": v(3.76, -3.76) * mm});
            skLineSegment(sketch, "E10.0.8.5", {"start": v(1.88, -3.76) * mm, "end": v(3.76, -3.76) * mm});
            skLineSegment(sketch, "E10.0.8.6", {"start": v(1.88, -1.88) * mm, "end": v(3.76, -1.88) * mm});
            skLineSegment(sketch, "E10.1.0.0", {"start": v(7.53, -47.04) * mm, "end": v(7.53, -48.92) * mm});
            skLineSegment(sketch, "E10.1.0.4", {"start": v(9.4, -47.04) * mm, "end": v(9.4, -48.92) * mm});
            skLineSegment(sketch, "E10.1.0.5", {"start": v(7.53, -48.92) * mm, "end": v(9.4, -48.92) * mm});
            skLineSegment(sketch, "E10.1.0.6", {"start": v(7.53, -47.04) * mm, "end": v(9.4, -47.04) * mm});
            skLineSegment(sketch, "E10.1.2.0", {"start": v(7.53, -35.75) * mm, "end": v(7.53, -37.63) * mm});
            skLineSegment(sketch, "E10.1.2.4", {"start": v(9.4, -35.75) * mm, "end": v(9.4, -37.63) * mm});
            skLineSegment(sketch, "E10.1.2.5", {"start": v(7.53, -37.63) * mm, "end": v(9.4, -37.63) * mm});
            skLineSegment(sketch, "E10.1.2.6", {"start": v(7.53, -35.75) * mm, "end": v(9.4, -35.75) * mm});
            skLineSegment(sketch, "E10.1.3.0", {"start": v(7.53, -30.1) * mm, "end": v(7.53, -31.99) * mm});
            skLineSegment(sketch, "E10.1.3.4", {"start": v(9.4, -30.1) * mm, "end": v(9.4, -31.99) * mm});
            skLineSegment(sketch, "E10.1.3.5", {"start": v(7.53, -31.99) * mm, "end": v(9.4, -31.99) * mm});
            skLineSegment(sketch, "E10.1.3.6", {"start": v(7.53, -30.1) * mm, "end": v(9.4, -30.1) * mm});
            skLineSegment(sketch, "E10.1.5.0", {"start": v(7.53, -18.81) * mm, "end": v(7.53, -20.7) * mm});
            skLineSegment(sketch, "E10.1.5.4", {"start": v(9.4, -18.81) * mm, "end": v(9.4, -20.7) * mm});
            skLineSegment(sketch, "E10.1.5.5", {"start": v(7.53, -20.7) * mm, "end": v(9.4, -20.7) * mm});
            skLineSegment(sketch, "E10.1.5.6", {"start": v(7.53, -18.81) * mm, "end": v(9.4, -18.81) * mm});
            skLineSegment(sketch, "E10.1.6.0", {"start": v(7.53, -13.17) * mm, "end": v(7.53, -15.05) * mm});
            skLineSegment(sketch, "E10.1.6.4", {"start": v(9.4, -13.17) * mm, "end": v(9.4, -15.05) * mm});
            skLineSegment(sketch, "E10.1.6.5", {"start": v(7.53, -15.05) * mm, "end": v(9.4, -15.05) * mm});
            skLineSegment(sketch, "E10.1.6.6", {"start": v(7.53, -13.17) * mm, "end": v(9.4, -13.17) * mm});
            skLineSegment(sketch, "E10.1.8.0", {"start": v(7.53, -1.88) * mm, "end": v(7.53, -3.76) * mm});
            skLineSegment(sketch, "E10.1.8.4", {"start": v(9.4, -1.88) * mm, "end": v(9.4, -3.76) * mm});
            skLineSegment(sketch, "E10.1.8.5", {"start": v(7.53, -3.76) * mm, "end": v(9.4, -3.76) * mm});
            skLineSegment(sketch, "E10.1.8.6", {"start": v(7.53, -1.88) * mm, "end": v(9.4, -1.88) * mm});
            skLineSegment(sketch, "E10.2.0.0", {"start": v(13.17, -47.04) * mm, "end": v(13.17, -48.92) * mm});
            skLineSegment(sketch, "E10.2.0.4", {"start": v(15.05, -47.04) * mm, "end": v(15.05, -48.92) * mm});
            skLineSegment(sketch, "E10.2.0.5", {"start": v(13.17, -48.92) * mm, "end": v(15.05, -48.92) * mm});
            skLineSegment(sketch, "E10.2.0.6", {"start": v(13.17, -47.04) * mm, "end": v(15.05, -47.04) * mm});
            skLineSegment(sketch, "E10.2.1.0", {"start": v(13.17, -41.4) * mm, "end": v(13.17, -43.27) * mm});
            skLineSegment(sketch, "E10.2.1.4", {"start": v(15.05, -41.4) * mm, "end": v(15.05, -43.27) * mm});
            skLineSegment(sketch, "E10.2.1.5", {"start": v(13.17, -43.27) * mm, "end": v(15.05, -43.27) * mm});
            skLineSegment(sketch, "E10.2.1.6", {"start": v(13.17, -41.4) * mm, "end": v(15.05, -41.4) * mm});
            skLineSegment(sketch, "E10.2.2.0", {"start": v(13.17, -35.75) * mm, "end": v(13.17, -37.63) * mm});
            skLineSegment(sketch, "E10.2.2.4", {"start": v(15.05, -35.75) * mm, "end": v(15.05, -37.63) * mm});
            skLineSegment(sketch, "E10.2.2.5", {"start": v(13.17, -37.63) * mm, "end": v(15.05, -37.63) * mm});
            skLineSegment(sketch, "E10.2.2.6", {"start": v(13.17, -35.75) * mm, "end": v(15.05, -35.75) * mm});
            skLineSegment(sketch, "E10.2.3.0", {"start": v(13.17, -30.1) * mm, "end": v(13.17, -31.99) * mm});
            skLineSegment(sketch, "E10.2.3.4", {"start": v(15.05, -30.1) * mm, "end": v(15.05, -31.99) * mm});
            skLineSegment(sketch, "E10.2.3.5", {"start": v(13.17, -31.99) * mm, "end": v(15.05, -31.99) * mm});
            skLineSegment(sketch, "E10.2.3.6", {"start": v(13.17, -30.1) * mm, "end": v(15.05, -30.1) * mm});
            skLineSegment(sketch, "E10.2.4.0", {"start": v(13.17, -24.46) * mm, "end": v(13.17, -26.34) * mm});
            skLineSegment(sketch, "E10.2.4.4", {"start": v(15.05, -24.46) * mm, "end": v(15.05, -26.34) * mm});
            skLineSegment(sketch, "E10.2.4.5", {"start": v(13.17, -26.34) * mm, "end": v(15.05, -26.34) * mm});
            skLineSegment(sketch, "E10.2.4.6", {"start": v(13.17, -24.46) * mm, "end": v(15.05, -24.46) * mm});
            skLineSegment(sketch, "E10.2.5.0", {"start": v(13.17, -18.81) * mm, "end": v(13.17, -20.7) * mm});
            skLineSegment(sketch, "E10.2.5.4", {"start": v(15.05, -18.81) * mm, "end": v(15.05, -20.7) * mm});
            skLineSegment(sketch, "E10.2.5.5", {"start": v(13.17, -20.7) * mm, "end": v(15.05, -20.7) * mm});
            skLineSegment(sketch, "E10.2.5.6", {"start": v(13.17, -18.81) * mm, "end": v(15.05, -18.81) * mm});
            skLineSegment(sketch, "E10.2.6.0", {"start": v(13.17, -13.17) * mm, "end": v(13.17, -15.05) * mm});
            skLineSegment(sketch, "E10.2.6.4", {"start": v(15.05, -13.17) * mm, "end": v(15.05, -15.05) * mm});
            skLineSegment(sketch, "E10.2.6.5", {"start": v(13.17, -15.05) * mm, "end": v(15.05, -15.05) * mm});
            skLineSegment(sketch, "E10.2.6.6", {"start": v(13.17, -13.17) * mm, "end": v(15.05, -13.17) * mm});
            skLineSegment(sketch, "E10.2.7.0", {"start": v(13.17, -7.53) * mm, "end": v(13.17, -9.4) * mm});
            skLineSegment(sketch, "E10.2.7.4", {"start": v(15.05, -7.53) * mm, "end": v(15.05, -9.4) * mm});
            skLineSegment(sketch, "E10.2.7.5", {"start": v(13.17, -9.4) * mm, "end": v(15.05, -9.4) * mm});
            skLineSegment(sketch, "E10.2.7.6", {"start": v(13.17, -7.53) * mm, "end": v(15.05, -7.53) * mm});
            skLineSegment(sketch, "E10.2.8.0", {"start": v(13.17, -1.88) * mm, "end": v(13.17, -3.76) * mm});
            skLineSegment(sketch, "E10.2.8.4", {"start": v(15.05, -1.88) * mm, "end": v(15.05, -3.76) * mm});
            skLineSegment(sketch, "E10.2.8.5", {"start": v(13.17, -3.76) * mm, "end": v(15.05, -3.76) * mm});
            skLineSegment(sketch, "E10.2.8.6", {"start": v(13.17, -1.88) * mm, "end": v(15.05, -1.88) * mm});
            skLineSegment(sketch, "E10.3.0.0", {"start": v(18.81, -47.04) * mm, "end": v(18.81, -48.92) * mm});
            skLineSegment(sketch, "E10.3.0.4", {"start": v(20.7, -47.04) * mm, "end": v(20.7, -48.92) * mm});
            skLineSegment(sketch, "E10.3.0.5", {"start": v(18.81, -48.92) * mm, "end": v(20.7, -48.92) * mm});
            skLineSegment(sketch, "E10.3.0.6", {"start": v(18.81, -47.04) * mm, "end": v(20.7, -47.04) * mm});
            skLineSegment(sketch, "E10.3.1.0", {"start": v(18.81, -41.4) * mm, "end": v(18.81, -43.27) * mm});
            skLineSegment(sketch, "E10.3.1.4", {"start": v(20.7, -41.4) * mm, "end": v(20.7, -43.27) * mm});
            skLineSegment(sketch, "E10.3.1.5", {"start": v(18.81, -43.27) * mm, "end": v(20.7, -43.27) * mm});
            skLineSegment(sketch, "E10.3.1.6", {"start": v(18.81, -41.4) * mm, "end": v(20.7, -41.4) * mm});
            skLineSegment(sketch, "E10.3.2.0", {"start": v(18.81, -35.75) * mm, "end": v(18.81, -37.63) * mm});
            skLineSegment(sketch, "E10.3.2.4", {"start": v(20.7, -35.75) * mm, "end": v(20.7, -37.63) * mm});
            skLineSegment(sketch, "E10.3.2.5", {"start": v(18.81, -37.63) * mm, "end": v(20.7, -37.63) * mm});
            skLineSegment(sketch, "E10.3.2.6", {"start": v(18.81, -35.75) * mm, "end": v(20.7, -35.75) * mm});
            skLineSegment(sketch, "E10.3.6.0", {"start": v(18.81, -13.17) * mm, "end": v(18.81, -15.05) * mm});
            skLineSegment(sketch, "E10.3.6.4", {"start": v(20.7, -13.17) * mm, "end": v(20.7, -15.05) * mm});
            skLineSegment(sketch, "E10.3.6.5", {"start": v(18.81, -15.05) * mm, "end": v(20.7, -15.05) * mm});
            skLineSegment(sketch, "E10.3.6.6", {"start": v(18.81, -13.17) * mm, "end": v(20.7, -13.17) * mm});
            skLineSegment(sketch, "E10.3.7.0", {"start": v(18.81, -7.53) * mm, "end": v(18.81, -9.4) * mm});
            skLineSegment(sketch, "E10.3.7.4", {"start": v(20.7, -7.53) * mm, "end": v(20.7, -9.4) * mm});
            skLineSegment(sketch, "E10.3.7.5", {"start": v(18.81, -9.4) * mm, "end": v(20.7, -9.4) * mm});
            skLineSegment(sketch, "E10.3.7.6", {"start": v(18.81, -7.53) * mm, "end": v(20.7, -7.53) * mm});
            skLineSegment(sketch, "E10.3.8.0", {"start": v(18.81, -1.88) * mm, "end": v(18.81, -3.76) * mm});
            skLineSegment(sketch, "E10.3.8.4", {"start": v(20.7, -1.88) * mm, "end": v(20.7, -3.76) * mm});
            skLineSegment(sketch, "E10.3.8.5", {"start": v(18.81, -3.76) * mm, "end": v(20.7, -3.76) * mm});
            skLineSegment(sketch, "E10.3.8.6", {"start": v(18.81, -1.88) * mm, "end": v(20.7, -1.88) * mm});
            skLineSegment(sketch, "E10.4.0.0", {"start": v(24.46, -47.04) * mm, "end": v(24.46, -48.92) * mm});
            skLineSegment(sketch, "E10.4.0.4", {"start": v(26.34, -47.04) * mm, "end": v(26.34, -48.92) * mm});
            skLineSegment(sketch, "E10.4.0.5", {"start": v(24.46, -48.92) * mm, "end": v(26.34, -48.92) * mm});
            skLineSegment(sketch, "E10.4.0.6", {"start": v(24.46, -47.04) * mm, "end": v(26.34, -47.04) * mm});
            skLineSegment(sketch, "E10.4.2.0", {"start": v(24.46, -35.75) * mm, "end": v(24.46, -37.63) * mm});
            skLineSegment(sketch, "E10.4.2.4", {"start": v(26.34, -35.75) * mm, "end": v(26.34, -37.63) * mm});
            skLineSegment(sketch, "E10.4.2.5", {"start": v(24.46, -37.63) * mm, "end": v(26.34, -37.63) * mm});
            skLineSegment(sketch, "E10.4.2.6", {"start": v(24.46, -35.75) * mm, "end": v(26.34, -35.75) * mm});
            skLineSegment(sketch, "E10.4.6.0", {"start": v(24.46, -13.17) * mm, "end": v(24.46, -15.05) * mm});
            skLineSegment(sketch, "E10.4.6.4", {"start": v(26.34, -13.17) * mm, "end": v(26.34, -15.05) * mm});
            skLineSegment(sketch, "E10.4.6.5", {"start": v(24.46, -15.05) * mm, "end": v(26.34, -15.05) * mm});
            skLineSegment(sketch, "E10.4.6.6", {"start": v(24.46, -13.17) * mm, "end": v(26.34, -13.17) * mm});
            skLineSegment(sketch, "E10.4.8.0", {"start": v(24.46, -1.88) * mm, "end": v(24.46, -3.76) * mm});
            skLineSegment(sketch, "E10.4.8.4", {"start": v(26.34, -1.88) * mm, "end": v(26.34, -3.76) * mm});
            skLineSegment(sketch, "E10.4.8.5", {"start": v(24.46, -3.76) * mm, "end": v(26.34, -3.76) * mm});
            skLineSegment(sketch, "E10.4.8.6", {"start": v(24.46, -1.88) * mm, "end": v(26.34, -1.88) * mm});
            skLineSegment(sketch, "E10.5.0.0", {"start": v(30.1, -47.04) * mm, "end": v(30.1, -48.92) * mm});
            skLineSegment(sketch, "E10.5.0.4", {"start": v(31.99, -47.04) * mm, "end": v(31.99, -48.92) * mm});
            skLineSegment(sketch, "E10.5.0.5", {"start": v(30.1, -48.92) * mm, "end": v(31.99, -48.92) * mm});
            skLineSegment(sketch, "E10.5.0.6", {"start": v(30.1, -47.04) * mm, "end": v(31.99, -47.04) * mm});
            skLineSegment(sketch, "E10.5.1.0", {"start": v(30.1, -41.4) * mm, "end": v(30.1, -43.27) * mm});
            skLineSegment(sketch, "E10.5.1.4", {"start": v(31.99, -41.4) * mm, "end": v(31.99, -43.27) * mm});
            skLineSegment(sketch, "E10.5.1.5", {"start": v(30.1, -43.27) * mm, "end": v(31.99, -43.27) * mm});
            skLineSegment(sketch, "E10.5.1.6", {"start": v(30.1, -41.4) * mm, "end": v(31.99, -41.4) * mm});
            skLineSegment(sketch, "E10.5.2.0", {"start": v(30.1, -35.75) * mm, "end": v(30.1, -37.63) * mm});
            skLineSegment(sketch, "E10.5.2.4", {"start": v(31.99, -35.75) * mm, "end": v(31.99, -37.63) * mm});
            skLineSegment(sketch, "E10.5.2.5", {"start": v(30.1, -37.63) * mm, "end": v(31.99, -37.63) * mm});
            skLineSegment(sketch, "E10.5.2.6", {"start": v(30.1, -35.75) * mm, "end": v(31.99, -35.75) * mm});
            skLineSegment(sketch, "E10.5.6.0", {"start": v(30.1, -13.17) * mm, "end": v(30.1, -15.05) * mm});
            skLineSegment(sketch, "E10.5.6.4", {"start": v(31.99, -13.17) * mm, "end": v(31.99, -15.05) * mm});
            skLineSegment(sketch, "E10.5.6.5", {"start": v(30.1, -15.05) * mm, "end": v(31.99, -15.05) * mm});
            skLineSegment(sketch, "E10.5.6.6", {"start": v(30.1, -13.17) * mm, "end": v(31.99, -13.17) * mm});
            skLineSegment(sketch, "E10.5.7.0", {"start": v(30.1, -7.53) * mm, "end": v(30.1, -9.4) * mm});
            skLineSegment(sketch, "E10.5.7.4", {"start": v(31.99, -7.53) * mm, "end": v(31.99, -9.4) * mm});
            skLineSegment(sketch, "E10.5.7.5", {"start": v(30.1, -9.4) * mm, "end": v(31.99, -9.4) * mm});
            skLineSegment(sketch, "E10.5.7.6", {"start": v(30.1, -7.53) * mm, "end": v(31.99, -7.53) * mm});
            skLineSegment(sketch, "E10.5.8.0", {"start": v(30.1, -1.88) * mm, "end": v(30.1, -3.76) * mm});
            skLineSegment(sketch, "E10.5.8.4", {"start": v(31.99, -1.88) * mm, "end": v(31.99, -3.76) * mm});
            skLineSegment(sketch, "E10.5.8.5", {"start": v(30.1, -3.76) * mm, "end": v(31.99, -3.76) * mm});
            skLineSegment(sketch, "E10.5.8.6", {"start": v(30.1, -1.88) * mm, "end": v(31.99, -1.88) * mm});
            skLineSegment(sketch, "E10.6.0.0", {"start": v(35.75, -47.04) * mm, "end": v(35.75, -48.92) * mm});
            skLineSegment(sketch, "E10.6.0.4", {"start": v(37.63, -47.04) * mm, "end": v(37.63, -48.92) * mm});
            skLineSegment(sketch, "E10.6.0.5", {"start": v(35.75, -48.92) * mm, "end": v(37.63, -48.92) * mm});
            skLineSegment(sketch, "E10.6.0.6", {"start": v(35.75, -47.04) * mm, "end": v(37.63, -47.04) * mm});
            skLineSegment(sketch, "E10.6.1.0", {"start": v(35.75, -41.4) * mm, "end": v(35.75, -43.27) * mm});
            skLineSegment(sketch, "E10.6.1.4", {"start": v(37.63, -41.4) * mm, "end": v(37.63, -43.27) * mm});
            skLineSegment(sketch, "E10.6.1.5", {"start": v(35.75, -43.27) * mm, "end": v(37.63, -43.27) * mm});
            skLineSegment(sketch, "E10.6.1.6", {"start": v(35.75, -41.4) * mm, "end": v(37.63, -41.4) * mm});
            skLineSegment(sketch, "E10.6.2.0", {"start": v(35.75, -35.75) * mm, "end": v(35.75, -37.63) * mm});
            skLineSegment(sketch, "E10.6.2.4", {"start": v(37.63, -35.75) * mm, "end": v(37.63, -37.63) * mm});
            skLineSegment(sketch, "E10.6.2.5", {"start": v(35.75, -37.63) * mm, "end": v(37.63, -37.63) * mm});
            skLineSegment(sketch, "E10.6.2.6", {"start": v(35.75, -35.75) * mm, "end": v(37.63, -35.75) * mm});
            skLineSegment(sketch, "E10.6.3.0", {"start": v(35.75, -30.1) * mm, "end": v(35.75, -31.99) * mm});
            skLineSegment(sketch, "E10.6.3.4", {"start": v(37.63, -30.1) * mm, "end": v(37.63, -31.99) * mm});
            skLineSegment(sketch, "E10.6.3.5", {"start": v(35.75, -31.99) * mm, "end": v(37.63, -31.99) * mm});
            skLineSegment(sketch, "E10.6.3.6", {"start": v(35.75, -30.1) * mm, "end": v(37.63, -30.1) * mm});
            skLineSegment(sketch, "E10.6.4.0", {"start": v(35.75, -24.46) * mm, "end": v(35.75, -26.34) * mm});
            skLineSegment(sketch, "E10.6.4.4", {"start": v(37.63, -24.46) * mm, "end": v(37.63, -26.34) * mm});
            skLineSegment(sketch, "E10.6.4.5", {"start": v(35.75, -26.34) * mm, "end": v(37.63, -26.34) * mm});
            skLineSegment(sketch, "E10.6.4.6", {"start": v(35.75, -24.46) * mm, "end": v(37.63, -24.46) * mm});
            skLineSegment(sketch, "E10.6.5.0", {"start": v(35.75, -18.81) * mm, "end": v(35.75, -20.7) * mm});
            skLineSegment(sketch, "E10.6.5.4", {"start": v(37.63, -18.81) * mm, "end": v(37.63, -20.7) * mm});
            skLineSegment(sketch, "E10.6.5.5", {"start": v(35.75, -20.7) * mm, "end": v(37.63, -20.7) * mm});
            skLineSegment(sketch, "E10.6.5.6", {"start": v(35.75, -18.81) * mm, "end": v(37.63, -18.81) * mm});
            skLineSegment(sketch, "E10.6.6.0", {"start": v(35.75, -13.17) * mm, "end": v(35.75, -15.05) * mm});
            skLineSegment(sketch, "E10.6.6.4", {"start": v(37.63, -13.17) * mm, "end": v(37.63, -15.05) * mm});
            skLineSegment(sketch, "E10.6.6.5", {"start": v(35.75, -15.05) * mm, "end": v(37.63, -15.05) * mm});
            skLineSegment(sketch, "E10.6.6.6", {"start": v(35.75, -13.17) * mm, "end": v(37.63, -13.17) * mm});
            skLineSegment(sketch, "E10.6.7.0", {"start": v(35.75, -7.53) * mm, "end": v(35.75, -9.4) * mm});
            skLineSegment(sketch, "E10.6.7.4", {"start": v(37.63, -7.53) * mm, "end": v(37.63, -9.4) * mm});
            skLineSegment(sketch, "E10.6.7.5", {"start": v(35.75, -9.4) * mm, "end": v(37.63, -9.4) * mm});
            skLineSegment(sketch, "E10.6.7.6", {"start": v(35.75, -7.53) * mm, "end": v(37.63, -7.53) * mm});
            skLineSegment(sketch, "E10.6.8.0", {"start": v(35.75, -1.88) * mm, "end": v(35.75, -3.76) * mm});
            skLineSegment(sketch, "E10.6.8.4", {"start": v(37.63, -1.88) * mm, "end": v(37.63, -3.76) * mm});
            skLineSegment(sketch, "E10.6.8.5", {"start": v(35.75, -3.76) * mm, "end": v(37.63, -3.76) * mm});
            skLineSegment(sketch, "E10.6.8.6", {"start": v(35.75, -1.88) * mm, "end": v(37.63, -1.88) * mm});
            skLineSegment(sketch, "E10.7.0.0", {"start": v(41.4, -47.04) * mm, "end": v(41.4, -48.92) * mm});
            skLineSegment(sketch, "E10.7.0.4", {"start": v(43.27, -47.04) * mm, "end": v(43.27, -48.92) * mm});
            skLineSegment(sketch, "E10.7.0.5", {"start": v(41.4, -48.92) * mm, "end": v(43.27, -48.92) * mm});
            skLineSegment(sketch, "E10.7.0.6", {"start": v(41.4, -47.04) * mm, "end": v(43.27, -47.04) * mm});
            skLineSegment(sketch, "E10.7.2.0", {"start": v(41.4, -35.75) * mm, "end": v(41.4, -37.63) * mm});
            skLineSegment(sketch, "E10.7.2.4", {"start": v(43.27, -35.75) * mm, "end": v(43.27, -37.63) * mm});
            skLineSegment(sketch, "E10.7.2.5", {"start": v(41.4, -37.63) * mm, "end": v(43.27, -37.63) * mm});
            skLineSegment(sketch, "E10.7.2.6", {"start": v(41.4, -35.75) * mm, "end": v(43.27, -35.75) * mm});
            skLineSegment(sketch, "E10.7.3.0", {"start": v(41.4, -30.1) * mm, "end": v(41.4, -31.99) * mm});
            skLineSegment(sketch, "E10.7.3.4", {"start": v(43.27, -30.1) * mm, "end": v(43.27, -31.99) * mm});
            skLineSegment(sketch, "E10.7.3.5", {"start": v(41.4, -31.99) * mm, "end": v(43.27, -31.99) * mm});
            skLineSegment(sketch, "E10.7.3.6", {"start": v(41.4, -30.1) * mm, "end": v(43.27, -30.1) * mm});
            skLineSegment(sketch, "E10.7.5.0", {"start": v(41.4, -18.81) * mm, "end": v(41.4, -20.7) * mm});
            skLineSegment(sketch, "E10.7.5.4", {"start": v(43.27, -18.81) * mm, "end": v(43.27, -20.7) * mm});
            skLineSegment(sketch, "E10.7.5.5", {"start": v(41.4, -20.7) * mm, "end": v(43.27, -20.7) * mm});
            skLineSegment(sketch, "E10.7.5.6", {"start": v(41.4, -18.81) * mm, "end": v(43.27, -18.81) * mm});
            skLineSegment(sketch, "E10.7.6.0", {"start": v(41.4, -13.17) * mm, "end": v(41.4, -15.05) * mm});
            skLineSegment(sketch, "E10.7.6.4", {"start": v(43.27, -13.17) * mm, "end": v(43.27, -15.05) * mm});
            skLineSegment(sketch, "E10.7.6.5", {"start": v(41.4, -15.05) * mm, "end": v(43.27, -15.05) * mm});
            skLineSegment(sketch, "E10.7.6.6", {"start": v(41.4, -13.17) * mm, "end": v(43.27, -13.17) * mm});
            skLineSegment(sketch, "E10.7.8.0", {"start": v(41.4, -1.88) * mm, "end": v(41.4, -3.76) * mm});
            skLineSegment(sketch, "E10.7.8.4", {"start": v(43.27, -1.88) * mm, "end": v(43.27, -3.76) * mm});
            skLineSegment(sketch, "E10.7.8.5", {"start": v(41.4, -3.76) * mm, "end": v(43.27, -3.76) * mm});
            skLineSegment(sketch, "E10.7.8.6", {"start": v(41.4, -1.88) * mm, "end": v(43.27, -1.88) * mm});
            skLineSegment(sketch, "E10.8.0.0", {"start": v(47.04, -47.04) * mm, "end": v(47.04, -48.92) * mm});
            skLineSegment(sketch, "E10.8.0.4", {"start": v(48.92, -47.04) * mm, "end": v(48.92, -48.92) * mm});
            skLineSegment(sketch, "E10.8.0.5", {"start": v(47.04, -48.92) * mm, "end": v(48.92, -48.92) * mm});
            skLineSegment(sketch, "E10.8.0.6", {"start": v(47.04, -47.04) * mm, "end": v(48.92, -47.04) * mm});
            skLineSegment(sketch, "E10.8.1.0", {"start": v(47.04, -41.4) * mm, "end": v(47.04, -43.27) * mm});
            skLineSegment(sketch, "E10.8.1.4", {"start": v(48.92, -41.4) * mm, "end": v(48.92, -43.27) * mm});
            skLineSegment(sketch, "E10.8.1.5", {"start": v(47.04, -43.27) * mm, "end": v(48.92, -43.27) * mm});
            skLineSegment(sketch, "E10.8.1.6", {"start": v(47.04, -41.4) * mm, "end": v(48.92, -41.4) * mm});
            skLineSegment(sketch, "E10.8.2.0", {"start": v(47.04, -35.75) * mm, "end": v(47.04, -37.63) * mm});
            skLineSegment(sketch, "E10.8.2.4", {"start": v(48.92, -35.75) * mm, "end": v(48.92, -37.63) * mm});
            skLineSegment(sketch, "E10.8.2.5", {"start": v(47.04, -37.63) * mm, "end": v(48.92, -37.63) * mm});
            skLineSegment(sketch, "E10.8.2.6", {"start": v(47.04, -35.75) * mm, "end": v(48.92, -35.75) * mm});
            skLineSegment(sketch, "E10.8.3.0", {"start": v(47.04, -30.1) * mm, "end": v(47.04, -31.99) * mm});
            skLineSegment(sketch, "E10.8.3.4", {"start": v(48.92, -30.1) * mm, "end": v(48.92, -31.99) * mm});
            skLineSegment(sketch, "E10.8.3.5", {"start": v(47.04, -31.99) * mm, "end": v(48.92, -31.99) * mm});
            skLineSegment(sketch, "E10.8.3.6", {"start": v(47.04, -30.1) * mm, "end": v(48.92, -30.1) * mm});
            skLineSegment(sketch, "E10.8.4.0", {"start": v(47.04, -24.46) * mm, "end": v(47.04, -26.34) * mm});
            skLineSegment(sketch, "E10.8.4.4", {"start": v(48.92, -24.46) * mm, "end": v(48.92, -26.34) * mm});
            skLineSegment(sketch, "E10.8.4.5", {"start": v(47.04, -26.34) * mm, "end": v(48.92, -26.34) * mm});
            skLineSegment(sketch, "E10.8.4.6", {"start": v(47.04, -24.46) * mm, "end": v(48.92, -24.46) * mm});
            skLineSegment(sketch, "E10.8.5.0", {"start": v(47.04, -18.81) * mm, "end": v(47.04, -20.7) * mm});
            skLineSegment(sketch, "E10.8.5.4", {"start": v(48.92, -18.81) * mm, "end": v(48.92, -20.7) * mm});
            skLineSegment(sketch, "E10.8.5.5", {"start": v(47.04, -20.7) * mm, "end": v(48.92, -20.7) * mm});
            skLineSegment(sketch, "E10.8.5.6", {"start": v(47.04, -18.81) * mm, "end": v(48.92, -18.81) * mm});
            skLineSegment(sketch, "E10.8.6.0", {"start": v(47.04, -13.17) * mm, "end": v(47.04, -15.05) * mm});
            skLineSegment(sketch, "E10.8.6.4", {"start": v(48.92, -13.17) * mm, "end": v(48.92, -15.05) * mm});
            skLineSegment(sketch, "E10.8.6.5", {"start": v(47.04, -15.05) * mm, "end": v(48.92, -15.05) * mm});
            skLineSegment(sketch, "E10.8.6.6", {"start": v(47.04, -13.17) * mm, "end": v(48.92, -13.17) * mm});
            skLineSegment(sketch, "E10.8.7.0", {"start": v(47.04, -7.53) * mm, "end": v(47.04, -9.4) * mm});
            skLineSegment(sketch, "E10.8.7.4", {"start": v(48.92, -7.53) * mm, "end": v(48.92, -9.4) * mm});
            skLineSegment(sketch, "E10.8.7.5", {"start": v(47.04, -9.4) * mm, "end": v(48.92, -9.4) * mm});
            skLineSegment(sketch, "E10.8.7.6", {"start": v(47.04, -7.53) * mm, "end": v(48.92, -7.53) * mm});
            skLineSegment(sketch, "E10.8.8.0", {"start": v(47.04, -1.88) * mm, "end": v(47.04, -3.76) * mm});
            skLineSegment(sketch, "E10.8.8.4", {"start": v(48.92, -1.88) * mm, "end": v(48.92, -3.76) * mm});
            skLineSegment(sketch, "E10.8.8.5", {"start": v(47.04, -3.76) * mm, "end": v(48.92, -3.76) * mm});
            skLineSegment(sketch, "E10.8.8.6", {"start": v(47.04, -1.88) * mm, "end": v(48.92, -1.88) * mm});
            skLineSegment(sketch, "E10.direction1", {"start": v(1.88, -48.92) * mm, "end": v(7.53, -48.92) * mm, "construction": true});
            skLineSegment(sketch, "E10.direction2", {"start": v(1.88, -48.92) * mm, "end": v(1.88, -43.27) * mm, "construction": true});
            skSolve(sketch);
        }
        {
            var Q0;
            Q0 = qSketchRegion(id + "F4", true);
            extrude(context, id + "F5", {"entities" : qUnion([Q0]), "operationType" : NewBodyOperationType.REMOVE, "endBound" : BoundingType.THROUGH_ALL, "oppositeDirection" : true, "depth" : 25.4 * mm});
        }
        {
            var Q0;
            Q0=makeQuery(id+"F1.opExtrude","SWEPT_FACE",FACE,{"disambiguationData":[OSD([sQuery(id+"F0.wireOp",EDGE,"E0.left")])]});
            var sketch = newSketch(context, id + "F6", { "sketchPlane" : qUnion([Q0])});
            skLineSegment(sketch, "E11.bottom", {"start": v(16.93, 33.87) * mm, "end": v(33.87, 33.87) * mm});
            skLineSegment(sketch, "E11.top", {"start": v(16.93, 16.93) * mm, "end": v(33.87, 16.93) * mm});
            skLineSegment(sketch, "E11.left", {"start": v(16.93, 33.87) * mm, "end": v(16.93, 16.93) * mm});
            skLineSegment(sketch, "E11.right", {"start": v(33.87, 33.87) * mm, "end": v(33.87, 16.93) * mm});
            skLineSegment(sketch, "E12.bottom", {"start": v(5.64, 11.29) * mm, "end": v(11.29, 11.29) * mm});
            skLineSegment(sketch, "E12.top", {"start": v(5.64, 5.64) * mm, "end": v(11.29, 5.64) * mm});
            skLineSegment(sketch, "E12.left", {"start": v(5.64, 11.29) * mm, "end": v(5.64, 5.64) * mm});
            skLineSegment(sketch, "E12.right", {"start": v(11.29, 11.29) * mm, "end": v(11.29, 5.64) * mm});
            skLineSegment(sketch, "E13.0.1.4", {"start": v(5.64, 28.22) * mm, "end": v(11.29, 28.22) * mm});
            skLineSegment(sketch, "E13.0.1.5", {"start": v(5.64, 22.58) * mm, "end": v(11.29, 22.58) * mm});
            skLineSegment(sketch, "E13.0.1.6", {"start": v(5.64, 28.22) * mm, "end": v(5.64, 22.58) * mm});
            skLineSegment(sketch, "E13.0.1.7", {"start": v(11.29, 28.22) * mm, "end": v(11.29, 22.58) * mm});
            skLineSegment(sketch, "E13.0.2.4", {"start": v(5.64, 45.16) * mm, "end": v(11.29, 45.16) * mm});
            skLineSegment(sketch, "E13.0.2.5", {"start": v(5.64, 39.51) * mm, "end": v(11.29, 39.51) * mm});
            skLineSegment(sketch, "E13.0.2.6", {"start": v(5.64, 45.16) * mm, "end": v(5.64, 39.51) * mm});
            skLineSegment(sketch, "E13.0.2.7", {"start": v(11.29, 45.16) * mm, "end": v(11.29, 39.51) * mm});
            skLineSegment(sketch, "E13.1.0.4", {"start": v(22.58, 11.29) * mm, "end": v(28.22, 11.29) * mm});
            skLineSegment(sketch, "E13.1.0.5", {"start": v(22.58, 5.64) * mm, "end": v(28.22, 5.64) * mm});
            skLineSegment(sketch, "E13.1.0.6", {"start": v(22.58, 11.29) * mm, "end": v(22.58, 5.64) * mm});
            skLineSegment(sketch, "E13.1.0.7", {"start": v(28.22, 11.29) * mm, "end": v(28.22, 5.64) * mm});
            skLineSegment(sketch, "E13.1.2.4", {"start": v(22.58, 45.16) * mm, "end": v(28.22, 45.16) * mm});
            skLineSegment(sketch, "E13.1.2.5", {"start": v(22.58, 39.51) * mm, "end": v(28.22, 39.51) * mm});
            skLineSegment(sketch, "E13.1.2.6", {"start": v(22.58, 45.16) * mm, "end": v(22.58, 39.51) * mm});
            skLineSegment(sketch, "E13.1.2.7", {"start": v(28.22, 45.16) * mm, "end": v(28.22, 39.51) * mm});
            skLineSegment(sketch, "E13.2.0.4", {"start": v(39.51, 11.29) * mm, "end": v(45.16, 11.29) * mm});
            skLineSegment(sketch, "E13.2.0.5", {"start": v(39.51, 5.64) * mm, "end": v(45.16, 5.64) * mm});
            skLineSegment(sketch, "E13.2.0.6", {"start": v(39.51, 11.29) * mm, "end": v(39.51, 5.64) * mm});
            skLineSegment(sketch, "E13.2.0.7", {"start": v(45.16, 11.29) * mm, "end": v(45.16, 5.64) * mm});
            skLineSegment(sketch, "E13.2.1.4", {"start": v(39.51, 28.22) * mm, "end": v(45.16, 28.22) * mm});
            skLineSegment(sketch, "E13.2.1.5", {"start": v(39.51, 22.58) * mm, "end": v(45.16, 22.58) * mm});
            skLineSegment(sketch, "E13.2.1.6", {"start": v(39.51, 28.22) * mm, "end": v(39.51, 22.58) * mm});
            skLineSegment(sketch, "E13.2.1.7", {"start": v(45.16, 28.22) * mm, "end": v(45.16, 22.58) * mm});
            skLineSegment(sketch, "E13.2.2.4", {"start": v(39.51, 45.16) * mm, "end": v(45.16, 45.16) * mm});
            skLineSegment(sketch, "E13.2.2.5", {"start": v(39.51, 39.51) * mm, "end": v(45.16, 39.51) * mm});
            skLineSegment(sketch, "E13.2.2.6", {"start": v(39.51, 45.16) * mm, "end": v(39.51, 39.51) * mm});
            skLineSegment(sketch, "E13.2.2.7", {"start": v(45.16, 45.16) * mm, "end": v(45.16, 39.51) * mm});
            skLineSegment(sketch, "E13.direction1", {"start": v(11.29, 5.64) * mm, "end": v(28.22, 5.64) * mm, "construction": true});
            skLineSegment(sketch, "E13.direction2", {"start": v(11.29, 5.64) * mm, "end": v(11.29, 22.58) * mm, "construction": true});
            skLineSegment(sketch, "E14.bottom", {"start": v(1.88, 3.76) * mm, "end": v(3.76, 3.76) * mm});
            skLineSegment(sketch, "E14.top", {"start": v(1.88, 1.88) * mm, "end": v(3.76, 1.88) * mm});
            skLineSegment(sketch, "E14.left", {"start": v(1.88, 3.76) * mm, "end": v(1.88, 1.88) * mm});
            skLineSegment(sketch, "E14.right", {"start": v(3.76, 3.76) * mm, "end": v(3.76, 1.88) * mm});
            skLineSegment(sketch, "E15.0.1.0", {"start": v(1.88, 9.4) * mm, "end": v(3.76, 9.4) * mm});
            skLineSegment(sketch, "E15.0.1.3", {"start": v(1.88, 9.4) * mm, "end": v(1.88, 7.53) * mm});
            skLineSegment(sketch, "E15.0.1.4", {"start": v(3.76, 9.4) * mm, "end": v(3.76, 7.53) * mm});
            skLineSegment(sketch, "E15.0.1.6", {"start": v(1.88, 7.53) * mm, "end": v(3.76, 7.53) * mm});
            skLineSegment(sketch, "E15.0.2.0", {"start": v(1.88, 15.05) * mm, "end": v(3.76, 15.05) * mm});
            skLineSegment(sketch, "E15.0.2.3", {"start": v(1.88, 15.05) * mm, "end": v(1.88, 13.17) * mm});
            skLineSegment(sketch, "E15.0.2.4", {"start": v(3.76, 15.05) * mm, "end": v(3.76, 13.17) * mm});
            skLineSegment(sketch, "E15.0.2.6", {"start": v(1.88, 13.17) * mm, "end": v(3.76, 13.17) * mm});
            skLineSegment(sketch, "E15.0.3.0", {"start": v(1.88, 20.7) * mm, "end": v(3.76, 20.7) * mm});
            skLineSegment(sketch, "E15.0.3.3", {"start": v(1.88, 20.7) * mm, "end": v(1.88, 18.81) * mm});
            skLineSegment(sketch, "E15.0.3.4", {"start": v(3.76, 20.7) * mm, "end": v(3.76, 18.81) * mm});
            skLineSegment(sketch, "E15.0.3.6", {"start": v(1.88, 18.81) * mm, "end": v(3.76, 18.81) * mm});
            skLineSegment(sketch, "E15.0.4.0", {"start": v(1.88, 26.34) * mm, "end": v(3.76, 26.34) * mm});
            skLineSegment(sketch, "E15.0.4.3", {"start": v(1.88, 26.34) * mm, "end": v(1.88, 24.46) * mm});
            skLineSegment(sketch, "E15.0.4.4", {"start": v(3.76, 26.34) * mm, "end": v(3.76, 24.46) * mm});
            skLineSegment(sketch, "E15.0.4.6", {"start": v(1.88, 24.46) * mm, "end": v(3.76, 24.46) * mm});
            skLineSegment(sketch, "E15.0.5.0", {"start": v(1.88, 31.99) * mm, "end": v(3.76, 31.99) * mm});
            skLineSegment(sketch, "E15.0.5.3", {"start": v(1.88, 31.99) * mm, "end": v(1.88, 30.1) * mm});
            skLineSegment(sketch, "E15.0.5.4", {"start": v(3.76, 31.99) * mm, "end": v(3.76, 30.1) * mm});
            skLineSegment(sketch, "E15.0.5.6", {"start": v(1.88, 30.1) * mm, "end": v(3.76, 30.1) * mm});
            skLineSegment(sketch, "E15.0.6.0", {"start": v(1.88, 37.63) * mm, "end": v(3.76, 37.63) * mm});
            skLineSegment(sketch, "E15.0.6.3", {"start": v(1.88, 37.63) * mm, "end": v(1.88, 35.75) * mm});
            skLineSegment(sketch, "E15.0.6.4", {"start": v(3.76, 37.63) * mm, "end": v(3.76, 35.75) * mm});
            skLineSegment(sketch, "E15.0.6.6", {"start": v(1.88, 35.75) * mm, "end": v(3.76, 35.75) * mm});
            skLineSegment(sketch, "E15.0.7.0", {"start": v(1.88, 43.27) * mm, "end": v(3.76, 43.27) * mm});
            skLineSegment(sketch, "E15.0.7.3", {"start": v(1.88, 43.27) * mm, "end": v(1.88, 41.4) * mm});
            skLineSegment(sketch, "E15.0.7.4", {"start": v(3.76, 43.27) * mm, "end": v(3.76, 41.4) * mm});
            skLineSegment(sketch, "E15.0.7.6", {"start": v(1.88, 41.4) * mm, "end": v(3.76, 41.4) * mm});
            skLineSegment(sketch, "E15.0.8.0", {"start": v(1.88, 48.92) * mm, "end": v(3.76, 48.92) * mm});
            skLineSegment(sketch, "E15.0.8.3", {"start": v(1.88, 48.92) * mm, "end": v(1.88, 47.04) * mm});
            skLineSegment(sketch, "E15.0.8.4", {"start": v(3.76, 48.92) * mm, "end": v(3.76, 47.04) * mm});
            skLineSegment(sketch, "E15.0.8.6", {"start": v(1.88, 47.04) * mm, "end": v(3.76, 47.04) * mm});
            skLineSegment(sketch, "E15.1.0.0", {"start": v(7.53, 3.76) * mm, "end": v(9.4, 3.76) * mm});
            skLineSegment(sketch, "E15.1.0.3", {"start": v(7.53, 3.76) * mm, "end": v(7.53, 1.88) * mm});
            skLineSegment(sketch, "E15.1.0.4", {"start": v(9.4, 3.76) * mm, "end": v(9.4, 1.88) * mm});
            skLineSegment(sketch, "E15.1.0.6", {"start": v(7.53, 1.88) * mm, "end": v(9.4, 1.88) * mm});
            skLineSegment(sketch, "E15.1.2.0", {"start": v(7.53, 15.05) * mm, "end": v(9.4, 15.05) * mm});
            skLineSegment(sketch, "E15.1.2.3", {"start": v(7.53, 15.05) * mm, "end": v(7.53, 13.17) * mm});
            skLineSegment(sketch, "E15.1.2.4", {"start": v(9.4, 15.05) * mm, "end": v(9.4, 13.17) * mm});
            skLineSegment(sketch, "E15.1.2.6", {"start": v(7.53, 13.17) * mm, "end": v(9.4, 13.17) * mm});
            skLineSegment(sketch, "E15.1.3.0", {"start": v(7.53, 20.7) * mm, "end": v(9.4, 20.7) * mm});
            skLineSegment(sketch, "E15.1.3.3", {"start": v(7.53, 20.7) * mm, "end": v(7.53, 18.81) * mm});
            skLineSegment(sketch, "E15.1.3.4", {"start": v(9.4, 20.7) * mm, "end": v(9.4, 18.81) * mm});
            skLineSegment(sketch, "E15.1.3.6", {"start": v(7.53, 18.81) * mm, "end": v(9.4, 18.81) * mm});
            skLineSegment(sketch, "E15.1.5.0", {"start": v(7.53, 31.99) * mm, "end": v(9.4, 31.99) * mm});
            skLineSegment(sketch, "E15.1.5.3", {"start": v(7.53, 31.99) * mm, "end": v(7.53, 30.1) * mm});
            skLineSegment(sketch, "E15.1.5.4", {"start": v(9.4, 31.99) * mm, "end": v(9.4, 30.1) * mm});
            skLineSegment(sketch, "E15.1.5.6", {"start": v(7.53, 30.1) * mm, "end": v(9.4, 30.1) * mm});
            skLineSegment(sketch, "E15.1.6.0", {"start": v(7.53, 37.63) * mm, "end": v(9.4, 37.63) * mm});
            skLineSegment(sketch, "E15.1.6.3", {"start": v(7.53, 37.63) * mm, "end": v(7.53, 35.75) * mm});
            skLineSegment(sketch, "E15.1.6.4", {"start": v(9.4, 37.63) * mm, "end": v(9.4, 35.75) * mm});
            skLineSegment(sketch, "E15.1.6.6", {"start": v(7.53, 35.75) * mm, "end": v(9.4, 35.75) * mm});
            skLineSegment(sketch, "E15.1.8.0", {"start": v(7.53, 48.92) * mm, "end": v(9.4, 48.92) * mm});
            skLineSegment(sketch, "E15.1.8.3", {"start": v(7.53, 48.92) * mm, "end": v(7.53, 47.04) * mm});
            skLineSegment(sketch, "E15.1.8.4", {"start": v(9.4, 48.92) * mm, "end": v(9.4, 47.04) * mm});
            skLineSegment(sketch, "E15.1.8.6", {"start": v(7.53, 47.04) * mm, "end": v(9.4, 47.04) * mm});
            skLineSegment(sketch, "E15.2.0.0", {"start": v(13.17, 3.76) * mm, "end": v(15.05, 3.76) * mm});
            skLineSegment(sketch, "E15.2.0.3", {"start": v(13.17, 3.76) * mm, "end": v(13.17, 1.88) * mm});
            skLineSegment(sketch, "E15.2.0.4", {"start": v(15.05, 3.76) * mm, "end": v(15.05, 1.88) * mm});
            skLineSegment(sketch, "E15.2.0.6", {"start": v(13.17, 1.88) * mm, "end": v(15.05, 1.88) * mm});
            skLineSegment(sketch, "E15.2.1.0", {"start": v(13.17, 9.4) * mm, "end": v(15.05, 9.4) * mm});
            skLineSegment(sketch, "E15.2.1.3", {"start": v(13.17, 9.4) * mm, "end": v(13.17, 7.53) * mm});
            skLineSegment(sketch, "E15.2.1.4", {"start": v(15.05, 9.4) * mm, "end": v(15.05, 7.53) * mm});
            skLineSegment(sketch, "E15.2.1.6", {"start": v(13.17, 7.53) * mm, "end": v(15.05, 7.53) * mm});
            skLineSegment(sketch, "E15.2.2.0", {"start": v(13.17, 15.05) * mm, "end": v(15.05, 15.05) * mm});
            skLineSegment(sketch, "E15.2.2.3", {"start": v(13.17, 15.05) * mm, "end": v(13.17, 13.17) * mm});
            skLineSegment(sketch, "E15.2.2.4", {"start": v(15.05, 15.05) * mm, "end": v(15.05, 13.17) * mm});
            skLineSegment(sketch, "E15.2.2.6", {"start": v(13.17, 13.17) * mm, "end": v(15.05, 13.17) * mm});
            skLineSegment(sketch, "E15.2.3.0", {"start": v(13.17, 20.7) * mm, "end": v(15.05, 20.7) * mm});
            skLineSegment(sketch, "E15.2.3.3", {"start": v(13.17, 20.7) * mm, "end": v(13.17, 18.81) * mm});
            skLineSegment(sketch, "E15.2.3.4", {"start": v(15.05, 20.7) * mm, "end": v(15.05, 18.81) * mm});
            skLineSegment(sketch, "E15.2.3.6", {"start": v(13.17, 18.81) * mm, "end": v(15.05, 18.81) * mm});
            skLineSegment(sketch, "E15.2.4.0", {"start": v(13.17, 26.34) * mm, "end": v(15.05, 26.34) * mm});
            skLineSegment(sketch, "E15.2.4.3", {"start": v(13.17, 26.34) * mm, "end": v(13.17, 24.46) * mm});
            skLineSegment(sketch, "E15.2.4.4", {"start": v(15.05, 26.34) * mm, "end": v(15.05, 24.46) * mm});
            skLineSegment(sketch, "E15.2.4.6", {"start": v(13.17, 24.46) * mm, "end": v(15.05, 24.46) * mm});
            skLineSegment(sketch, "E15.2.5.0", {"start": v(13.17, 31.99) * mm, "end": v(15.05, 31.99) * mm});
            skLineSegment(sketch, "E15.2.5.3", {"start": v(13.17, 31.99) * mm, "end": v(13.17, 30.1) * mm});
            skLineSegment(sketch, "E15.2.5.4", {"start": v(15.05, 31.99) * mm, "end": v(15.05, 30.1) * mm});
            skLineSegment(sketch, "E15.2.5.6", {"start": v(13.17, 30.1) * mm, "end": v(15.05, 30.1) * mm});
            skLineSegment(sketch, "E15.2.6.0", {"start": v(13.17, 37.63) * mm, "end": v(15.05, 37.63) * mm});
            skLineSegment(sketch, "E15.2.6.3", {"start": v(13.17, 37.63) * mm, "end": v(13.17, 35.75) * mm});
            skLineSegment(sketch, "E15.2.6.4", {"start": v(15.05, 37.63) * mm, "end": v(15.05, 35.75) * mm});
            skLineSegment(sketch, "E15.2.6.6", {"start": v(13.17, 35.75) * mm, "end": v(15.05, 35.75) * mm});
            skLineSegment(sketch, "E15.2.7.0", {"start": v(13.17, 43.27) * mm, "end": v(15.05, 43.27) * mm});
            skLineSegment(sketch, "E15.2.7.3", {"start": v(13.17, 43.27) * mm, "end": v(13.17, 41.4) * mm});
            skLineSegment(sketch, "E15.2.7.4", {"start": v(15.05, 43.27) * mm, "end": v(15.05, 41.4) * mm});
            skLineSegment(sketch, "E15.2.7.6", {"start": v(13.17, 41.4) * mm, "end": v(15.05, 41.4) * mm});
            skLineSegment(sketch, "E15.2.8.0", {"start": v(13.17, 48.92) * mm, "end": v(15.05, 48.92) * mm});
            skLineSegment(sketch, "E15.2.8.3", {"start": v(13.17, 48.92) * mm, "end": v(13.17, 47.04) * mm});
            skLineSegment(sketch, "E15.2.8.4", {"start": v(15.05, 48.92) * mm, "end": v(15.05, 47.04) * mm});
            skLineSegment(sketch, "E15.2.8.6", {"start": v(13.17, 47.04) * mm, "end": v(15.05, 47.04) * mm});
            skLineSegment(sketch, "E15.3.0.0", {"start": v(18.81, 3.76) * mm, "end": v(20.7, 3.76) * mm});
            skLineSegment(sketch, "E15.3.0.3", {"start": v(18.81, 3.76) * mm, "end": v(18.81, 1.88) * mm});
            skLineSegment(sketch, "E15.3.0.4", {"start": v(20.7, 3.76) * mm, "end": v(20.7, 1.88) * mm});
            skLineSegment(sketch, "E15.3.0.6", {"start": v(18.81, 1.88) * mm, "end": v(20.7, 1.88) * mm});
            skLineSegment(sketch, "E15.3.1.0", {"start": v(18.81, 9.4) * mm, "end": v(20.7, 9.4) * mm});
            skLineSegment(sketch, "E15.3.1.3", {"start": v(18.81, 9.4) * mm, "end": v(18.81, 7.53) * mm});
            skLineSegment(sketch, "E15.3.1.4", {"start": v(20.7, 9.4) * mm, "end": v(20.7, 7.53) * mm});
            skLineSegment(sketch, "E15.3.1.6", {"start": v(18.81, 7.53) * mm, "end": v(20.7, 7.53) * mm});
            skLineSegment(sketch, "E15.3.2.0", {"start": v(18.81, 15.05) * mm, "end": v(20.7, 15.05) * mm});
            skLineSegment(sketch, "E15.3.2.3", {"start": v(18.81, 15.05) * mm, "end": v(18.81, 13.17) * mm});
            skLineSegment(sketch, "E15.3.2.4", {"start": v(20.7, 15.05) * mm, "end": v(20.7, 13.17) * mm});
            skLineSegment(sketch, "E15.3.2.6", {"start": v(18.81, 13.17) * mm, "end": v(20.7, 13.17) * mm});
            skLineSegment(sketch, "E15.3.6.0", {"start": v(18.81, 37.63) * mm, "end": v(20.7, 37.63) * mm});
            skLineSegment(sketch, "E15.3.6.3", {"start": v(18.81, 37.63) * mm, "end": v(18.81, 35.75) * mm});
            skLineSegment(sketch, "E15.3.6.4", {"start": v(20.7, 37.63) * mm, "end": v(20.7, 35.75) * mm});
            skLineSegment(sketch, "E15.3.6.6", {"start": v(18.81, 35.75) * mm, "end": v(20.7, 35.75) * mm});
            skLineSegment(sketch, "E15.3.7.0", {"start": v(18.81, 43.27) * mm, "end": v(20.7, 43.27) * mm});
            skLineSegment(sketch, "E15.3.7.3", {"start": v(18.81, 43.27) * mm, "end": v(18.81, 41.4) * mm});
            skLineSegment(sketch, "E15.3.7.4", {"start": v(20.7, 43.27) * mm, "end": v(20.7, 41.4) * mm});
            skLineSegment(sketch, "E15.3.7.6", {"start": v(18.81, 41.4) * mm, "end": v(20.7, 41.4) * mm});
            skLineSegment(sketch, "E15.3.8.0", {"start": v(18.81, 48.92) * mm, "end": v(20.7, 48.92) * mm});
            skLineSegment(sketch, "E15.3.8.3", {"start": v(18.81, 48.92) * mm, "end": v(18.81, 47.04) * mm});
            skLineSegment(sketch, "E15.3.8.4", {"start": v(20.7, 48.92) * mm, "end": v(20.7, 47.04) * mm});
            skLineSegment(sketch, "E15.3.8.6", {"start": v(18.81, 47.04) * mm, "end": v(20.7, 47.04) * mm});
            skLineSegment(sketch, "E15.4.0.0", {"start": v(24.46, 3.76) * mm, "end": v(26.34, 3.76) * mm});
            skLineSegment(sketch, "E15.4.0.3", {"start": v(24.46, 3.76) * mm, "end": v(24.46, 1.88) * mm});
            skLineSegment(sketch, "E15.4.0.4", {"start": v(26.34, 3.76) * mm, "end": v(26.34, 1.88) * mm});
            skLineSegment(sketch, "E15.4.0.6", {"start": v(24.46, 1.88) * mm, "end": v(26.34, 1.88) * mm});
            skLineSegment(sketch, "E15.4.2.0", {"start": v(24.46, 15.05) * mm, "end": v(26.34, 15.05) * mm});
            skLineSegment(sketch, "E15.4.2.3", {"start": v(24.46, 15.05) * mm, "end": v(24.46, 13.17) * mm});
            skLineSegment(sketch, "E15.4.2.4", {"start": v(26.34, 15.05) * mm, "end": v(26.34, 13.17) * mm});
            skLineSegment(sketch, "E15.4.2.6", {"start": v(24.46, 13.17) * mm, "end": v(26.34, 13.17) * mm});
            skLineSegment(sketch, "E15.4.6.0", {"start": v(24.46, 37.63) * mm, "end": v(26.34, 37.63) * mm});
            skLineSegment(sketch, "E15.4.6.3", {"start": v(24.46, 37.63) * mm, "end": v(24.46, 35.75) * mm});
            skLineSegment(sketch, "E15.4.6.4", {"start": v(26.34, 37.63) * mm, "end": v(26.34, 35.75) * mm});
            skLineSegment(sketch, "E15.4.6.6", {"start": v(24.46, 35.75) * mm, "end": v(26.34, 35.75) * mm});
            skLineSegment(sketch, "E15.4.8.0", {"start": v(24.46, 48.92) * mm, "end": v(26.34, 48.92) * mm});
            skLineSegment(sketch, "E15.4.8.3", {"start": v(24.46, 48.92) * mm, "end": v(24.46, 47.04) * mm});
            skLineSegment(sketch, "E15.4.8.4", {"start": v(26.34, 48.92) * mm, "end": v(26.34, 47.04) * mm});
            skLineSegment(sketch, "E15.4.8.6", {"start": v(24.46, 47.04) * mm, "end": v(26.34, 47.04) * mm});
            skLineSegment(sketch, "E15.5.0.0", {"start": v(30.1, 3.76) * mm, "end": v(31.99, 3.76) * mm});
            skLineSegment(sketch, "E15.5.0.3", {"start": v(30.1, 3.76) * mm, "end": v(30.1, 1.88) * mm});
            skLineSegment(sketch, "E15.5.0.4", {"start": v(31.99, 3.76) * mm, "end": v(31.99, 1.88) * mm});
            skLineSegment(sketch, "E15.5.0.6", {"start": v(30.1, 1.88) * mm, "end": v(31.99, 1.88) * mm});
            skLineSegment(sketch, "E15.5.1.0", {"start": v(30.1, 9.4) * mm, "end": v(31.99, 9.4) * mm});
            skLineSegment(sketch, "E15.5.1.3", {"start": v(30.1, 9.4) * mm, "end": v(30.1, 7.53) * mm});
            skLineSegment(sketch, "E15.5.1.4", {"start": v(31.99, 9.4) * mm, "end": v(31.99, 7.53) * mm});
            skLineSegment(sketch, "E15.5.1.6", {"start": v(30.1, 7.53) * mm, "end": v(31.99, 7.53) * mm});
            skLineSegment(sketch, "E15.5.2.0", {"start": v(30.1, 15.05) * mm, "end": v(31.99, 15.05) * mm});
            skLineSegment(sketch, "E15.5.2.3", {"start": v(30.1, 15.05) * mm, "end": v(30.1, 13.17) * mm});
            skLineSegment(sketch, "E15.5.2.4", {"start": v(31.99, 15.05) * mm, "end": v(31.99, 13.17) * mm});
            skLineSegment(sketch, "E15.5.2.6", {"start": v(30.1, 13.17) * mm, "end": v(31.99, 13.17) * mm});
            skLineSegment(sketch, "E15.5.6.0", {"start": v(30.1, 37.63) * mm, "end": v(31.99, 37.63) * mm});
            skLineSegment(sketch, "E15.5.6.3", {"start": v(30.1, 37.63) * mm, "end": v(30.1, 35.75) * mm});
            skLineSegment(sketch, "E15.5.6.4", {"start": v(31.99, 37.63) * mm, "end": v(31.99, 35.75) * mm});
            skLineSegment(sketch, "E15.5.6.6", {"start": v(30.1, 35.75) * mm, "end": v(31.99, 35.75) * mm});
            skLineSegment(sketch, "E15.5.7.0", {"start": v(30.1, 43.27) * mm, "end": v(31.99, 43.27) * mm});
            skLineSegment(sketch, "E15.5.7.3", {"start": v(30.1, 43.27) * mm, "end": v(30.1, 41.4) * mm});
            skLineSegment(sketch, "E15.5.7.4", {"start": v(31.99, 43.27) * mm, "end": v(31.99, 41.4) * mm});
            skLineSegment(sketch, "E15.5.7.6", {"start": v(30.1, 41.4) * mm, "end": v(31.99, 41.4) * mm});
            skLineSegment(sketch, "E15.5.8.0", {"start": v(30.1, 48.92) * mm, "end": v(31.99, 48.92) * mm});
            skLineSegment(sketch, "E15.5.8.3", {"start": v(30.1, 48.92) * mm, "end": v(30.1, 47.04) * mm});
            skLineSegment(sketch, "E15.5.8.4", {"start": v(31.99, 48.92) * mm, "end": v(31.99, 47.04) * mm});
            skLineSegment(sketch, "E15.5.8.6", {"start": v(30.1, 47.04) * mm, "end": v(31.99, 47.04) * mm});
            skLineSegment(sketch, "E15.6.0.0", {"start": v(35.75, 3.76) * mm, "end": v(37.63, 3.76) * mm});
            skLineSegment(sketch, "E15.6.0.3", {"start": v(35.75, 3.76) * mm, "end": v(35.75, 1.88) * mm});
            skLineSegment(sketch, "E15.6.0.4", {"start": v(37.63, 3.76) * mm, "end": v(37.63, 1.88) * mm});
            skLineSegment(sketch, "E15.6.0.6", {"start": v(35.75, 1.88) * mm, "end": v(37.63, 1.88) * mm});
            skLineSegment(sketch, "E15.6.1.0", {"start": v(35.75, 9.4) * mm, "end": v(37.63, 9.4) * mm});
            skLineSegment(sketch, "E15.6.1.3", {"start": v(35.75, 9.4) * mm, "end": v(35.75, 7.53) * mm});
            skLineSegment(sketch, "E15.6.1.4", {"start": v(37.63, 9.4) * mm, "end": v(37.63, 7.53) * mm});
            skLineSegment(sketch, "E15.6.1.6", {"start": v(35.75, 7.53) * mm, "end": v(37.63, 7.53) * mm});
            skLineSegment(sketch, "E15.6.2.0", {"start": v(35.75, 15.05) * mm, "end": v(37.63, 15.05) * mm});
            skLineSegment(sketch, "E15.6.2.3", {"start": v(35.75, 15.05) * mm, "end": v(35.75, 13.17) * mm});
            skLineSegment(sketch, "E15.6.2.4", {"start": v(37.63, 15.05) * mm, "end": v(37.63, 13.17) * mm});
            skLineSegment(sketch, "E15.6.2.6", {"start": v(35.75, 13.17) * mm, "end": v(37.63, 13.17) * mm});
            skLineSegment(sketch, "E15.6.3.0", {"start": v(35.75, 20.7) * mm, "end": v(37.63, 20.7) * mm});
            skLineSegment(sketch, "E15.6.3.3", {"start": v(35.75, 20.7) * mm, "end": v(35.75, 18.81) * mm});
            skLineSegment(sketch, "E15.6.3.4", {"start": v(37.63, 20.7) * mm, "end": v(37.63, 18.81) * mm});
            skLineSegment(sketch, "E15.6.3.6", {"start": v(35.75, 18.81) * mm, "end": v(37.63, 18.81) * mm});
            skLineSegment(sketch, "E15.6.4.0", {"start": v(35.75, 26.34) * mm, "end": v(37.63, 26.34) * mm});
            skLineSegment(sketch, "E15.6.4.3", {"start": v(35.75, 26.34) * mm, "end": v(35.75, 24.46) * mm});
            skLineSegment(sketch, "E15.6.4.4", {"start": v(37.63, 26.34) * mm, "end": v(37.63, 24.46) * mm});
            skLineSegment(sketch, "E15.6.4.6", {"start": v(35.75, 24.46) * mm, "end": v(37.63, 24.46) * mm});
            skLineSegment(sketch, "E15.6.5.0", {"start": v(35.75, 31.99) * mm, "end": v(37.63, 31.99) * mm});
            skLineSegment(sketch, "E15.6.5.3", {"start": v(35.75, 31.99) * mm, "end": v(35.75, 30.1) * mm});
            skLineSegment(sketch, "E15.6.5.4", {"start": v(37.63, 31.99) * mm, "end": v(37.63, 30.1) * mm});
            skLineSegment(sketch, "E15.6.5.6", {"start": v(35.75, 30.1) * mm, "end": v(37.63, 30.1) * mm});
            skLineSegment(sketch, "E15.6.6.0", {"start": v(35.75, 37.63) * mm, "end": v(37.63, 37.63) * mm});
            skLineSegment(sketch, "E15.6.6.3", {"start": v(35.75, 37.63) * mm, "end": v(35.75, 35.75) * mm});
            skLineSegment(sketch, "E15.6.6.4", {"start": v(37.63, 37.63) * mm, "end": v(37.63, 35.75) * mm});
            skLineSegment(sketch, "E15.6.6.6", {"start": v(35.75, 35.75) * mm, "end": v(37.63, 35.75) * mm});
            skLineSegment(sketch, "E15.6.7.0", {"start": v(35.75, 43.27) * mm, "end": v(37.63, 43.27) * mm});
            skLineSegment(sketch, "E15.6.7.3", {"start": v(35.75, 43.27) * mm, "end": v(35.75, 41.4) * mm});
            skLineSegment(sketch, "E15.6.7.4", {"start": v(37.63, 43.27) * mm, "end": v(37.63, 41.4) * mm});
            skLineSegment(sketch, "E15.6.7.6", {"start": v(35.75, 41.4) * mm, "end": v(37.63, 41.4) * mm});
            skLineSegment(sketch, "E15.6.8.0", {"start": v(35.75, 48.92) * mm, "end": v(37.63, 48.92) * mm});
            skLineSegment(sketch, "E15.6.8.3", {"start": v(35.75, 48.92) * mm, "end": v(35.75, 47.04) * mm});
            skLineSegment(sketch, "E15.6.8.4", {"start": v(37.63, 48.92) * mm, "end": v(37.63, 47.04) * mm});
            skLineSegment(sketch, "E15.6.8.6", {"start": v(35.75, 47.04) * mm, "end": v(37.63, 47.04) * mm});
            skLineSegment(sketch, "E15.7.0.0", {"start": v(41.4, 3.76) * mm, "end": v(43.27, 3.76) * mm});
            skLineSegment(sketch, "E15.7.0.3", {"start": v(41.4, 3.76) * mm, "end": v(41.4, 1.88) * mm});
            skLineSegment(sketch, "E15.7.0.4", {"start": v(43.27, 3.76) * mm, "end": v(43.27, 1.88) * mm});
            skLineSegment(sketch, "E15.7.0.6", {"start": v(41.4, 1.88) * mm, "end": v(43.27, 1.88) * mm});
            skLineSegment(sketch, "E15.7.2.0", {"start": v(41.4, 15.05) * mm, "end": v(43.27, 15.05) * mm});
            skLineSegment(sketch, "E15.7.2.3", {"start": v(41.4, 15.05) * mm, "end": v(41.4, 13.17) * mm});
            skLineSegment(sketch, "E15.7.2.4", {"start": v(43.27, 15.05) * mm, "end": v(43.27, 13.17) * mm});
            skLineSegment(sketch, "E15.7.2.6", {"start": v(41.4, 13.17) * mm, "end": v(43.27, 13.17) * mm});
            skLineSegment(sketch, "E15.7.3.0", {"start": v(41.4, 20.7) * mm, "end": v(43.27, 20.7) * mm});
            skLineSegment(sketch, "E15.7.3.3", {"start": v(41.4, 20.7) * mm, "end": v(41.4, 18.81) * mm});
            skLineSegment(sketch, "E15.7.3.4", {"start": v(43.27, 20.7) * mm, "end": v(43.27, 18.81) * mm});
            skLineSegment(sketch, "E15.7.3.6", {"start": v(41.4, 18.81) * mm, "end": v(43.27, 18.81) * mm});
            skLineSegment(sketch, "E15.7.5.0", {"start": v(41.4, 31.99) * mm, "end": v(43.27, 31.99) * mm});
            skLineSegment(sketch, "E15.7.5.3", {"start": v(41.4, 31.99) * mm, "end": v(41.4, 30.1) * mm});
            skLineSegment(sketch, "E15.7.5.4", {"start": v(43.27, 31.99) * mm, "end": v(43.27, 30.1) * mm});
            skLineSegment(sketch, "E15.7.5.6", {"start": v(41.4, 30.1) * mm, "end": v(43.27, 30.1) * mm});
            skLineSegment(sketch, "E15.7.6.0", {"start": v(41.4, 37.63) * mm, "end": v(43.27, 37.63) * mm});
            skLineSegment(sketch, "E15.7.6.3", {"start": v(41.4, 37.63) * mm, "end": v(41.4, 35.75) * mm});
            skLineSegment(sketch, "E15.7.6.4", {"start": v(43.27, 37.63) * mm, "end": v(43.27, 35.75) * mm});
            skLineSegment(sketch, "E15.7.6.6", {"start": v(41.4, 35.75) * mm, "end": v(43.27, 35.75) * mm});
            skLineSegment(sketch, "E15.7.8.0", {"start": v(41.4, 48.92) * mm, "end": v(43.27, 48.92) * mm});
            skLineSegment(sketch, "E15.7.8.3", {"start": v(41.4, 48.92) * mm, "end": v(41.4, 47.04) * mm});
            skLineSegment(sketch, "E15.7.8.4", {"start": v(43.27, 48.92) * mm, "end": v(43.27, 47.04) * mm});
            skLineSegment(sketch, "E15.7.8.6", {"start": v(41.4, 47.04) * mm, "end": v(43.27, 47.04) * mm});
            skLineSegment(sketch, "E15.8.0.0", {"start": v(47.04, 3.76) * mm, "end": v(48.92, 3.76) * mm});
            skLineSegment(sketch, "E15.8.0.3", {"start": v(47.04, 3.76) * mm, "end": v(47.04, 1.88) * mm});
            skLineSegment(sketch, "E15.8.0.4", {"start": v(48.92, 3.76) * mm, "end": v(48.92, 1.88) * mm});
            skLineSegment(sketch, "E15.8.0.6", {"start": v(47.04, 1.88) * mm, "end": v(48.92, 1.88) * mm});
            skLineSegment(sketch, "E15.8.1.0", {"start": v(47.04, 9.4) * mm, "end": v(48.92, 9.4) * mm});
            skLineSegment(sketch, "E15.8.1.3", {"start": v(47.04, 9.4) * mm, "end": v(47.04, 7.53) * mm});
            skLineSegment(sketch, "E15.8.1.4", {"start": v(48.92, 9.4) * mm, "end": v(48.92, 7.53) * mm});
            skLineSegment(sketch, "E15.8.1.6", {"start": v(47.04, 7.53) * mm, "end": v(48.92, 7.53) * mm});
            skLineSegment(sketch, "E15.8.2.0", {"start": v(47.04, 15.05) * mm, "end": v(48.92, 15.05) * mm});
            skLineSegment(sketch, "E15.8.2.3", {"start": v(47.04, 15.05) * mm, "end": v(47.04, 13.17) * mm});
            skLineSegment(sketch, "E15.8.2.4", {"start": v(48.92, 15.05) * mm, "end": v(48.92, 13.17) * mm});
            skLineSegment(sketch, "E15.8.2.6", {"start": v(47.04, 13.17) * mm, "end": v(48.92, 13.17) * mm});
            skLineSegment(sketch, "E15.8.3.0", {"start": v(47.04, 20.7) * mm, "end": v(48.92, 20.7) * mm});
            skLineSegment(sketch, "E15.8.3.3", {"start": v(47.04, 20.7) * mm, "end": v(47.04, 18.81) * mm});
            skLineSegment(sketch, "E15.8.3.4", {"start": v(48.92, 20.7) * mm, "end": v(48.92, 18.81) * mm});
            skLineSegment(sketch, "E15.8.3.6", {"start": v(47.04, 18.81) * mm, "end": v(48.92, 18.81) * mm});
            skLineSegment(sketch, "E15.8.4.0", {"start": v(47.04, 26.34) * mm, "end": v(48.92, 26.34) * mm});
            skLineSegment(sketch, "E15.8.4.3", {"start": v(47.04, 26.34) * mm, "end": v(47.04, 24.46) * mm});
            skLineSegment(sketch, "E15.8.4.4", {"start": v(48.92, 26.34) * mm, "end": v(48.92, 24.46) * mm});
            skLineSegment(sketch, "E15.8.4.6", {"start": v(47.04, 24.46) * mm, "end": v(48.92, 24.46) * mm});
            skLineSegment(sketch, "E15.8.5.0", {"start": v(47.04, 31.99) * mm, "end": v(48.92, 31.99) * mm});
            skLineSegment(sketch, "E15.8.5.3", {"start": v(47.04, 31.99) * mm, "end": v(47.04, 30.1) * mm});
            skLineSegment(sketch, "E15.8.5.4", {"start": v(48.92, 31.99) * mm, "end": v(48.92, 30.1) * mm});
            skLineSegment(sketch, "E15.8.5.6", {"start": v(47.04, 30.1) * mm, "end": v(48.92, 30.1) * mm});
            skLineSegment(sketch, "E15.8.6.0", {"start": v(47.04, 37.63) * mm, "end": v(48.92, 37.63) * mm});
            skLineSegment(sketch, "E15.8.6.3", {"start": v(47.04, 37.63) * mm, "end": v(47.04, 35.75) * mm});
            skLineSegment(sketch, "E15.8.6.4", {"start": v(48.92, 37.63) * mm, "end": v(48.92, 35.75) * mm});
            skLineSegment(sketch, "E15.8.6.6", {"start": v(47.04, 35.75) * mm, "end": v(48.92, 35.75) * mm});
            skLineSegment(sketch, "E15.8.7.0", {"start": v(47.04, 43.27) * mm, "end": v(48.92, 43.27) * mm});
            skLineSegment(sketch, "E15.8.7.3", {"start": v(47.04, 43.27) * mm, "end": v(47.04, 41.4) * mm});
            skLineSegment(sketch, "E15.8.7.4", {"start": v(48.92, 43.27) * mm, "end": v(48.92, 41.4) * mm});
            skLineSegment(sketch, "E15.8.7.6", {"start": v(47.04, 41.4) * mm, "end": v(48.92, 41.4) * mm});
            skLineSegment(sketch, "E15.8.8.0", {"start": v(47.04, 48.92) * mm, "end": v(48.92, 48.92) * mm});
            skLineSegment(sketch, "E15.8.8.3", {"start": v(47.04, 48.92) * mm, "end": v(47.04, 47.04) * mm});
            skLineSegment(sketch, "E15.8.8.4", {"start": v(48.92, 48.92) * mm, "end": v(48.92, 47.04) * mm});
            skLineSegment(sketch, "E15.8.8.6", {"start": v(47.04, 47.04) * mm, "end": v(48.92, 47.04) * mm});
            skLineSegment(sketch, "E15.direction1", {"start": v(1.88, 3.76) * mm, "end": v(7.53, 3.76) * mm, "construction": true});
            skLineSegment(sketch, "E15.direction2", {"start": v(1.88, 3.76) * mm, "end": v(1.88, 9.4) * mm, "construction": true});
            skSolve(sketch);
        }
        {
            var Q0;
            Q0 = qSketchRegion(id + "F6", true);
            var Q1;
            Q1 = qSketchRegion(id + "F6", true);
            extrude(context, id + "F7", {"entities" : qUnion([Q0, Q1]), "operationType" : NewBodyOperationType.REMOVE, "endBound" : BoundingType.THROUGH_ALL, "oppositeDirection" : true, "depth" : 25.4 * mm});
        }
    });
